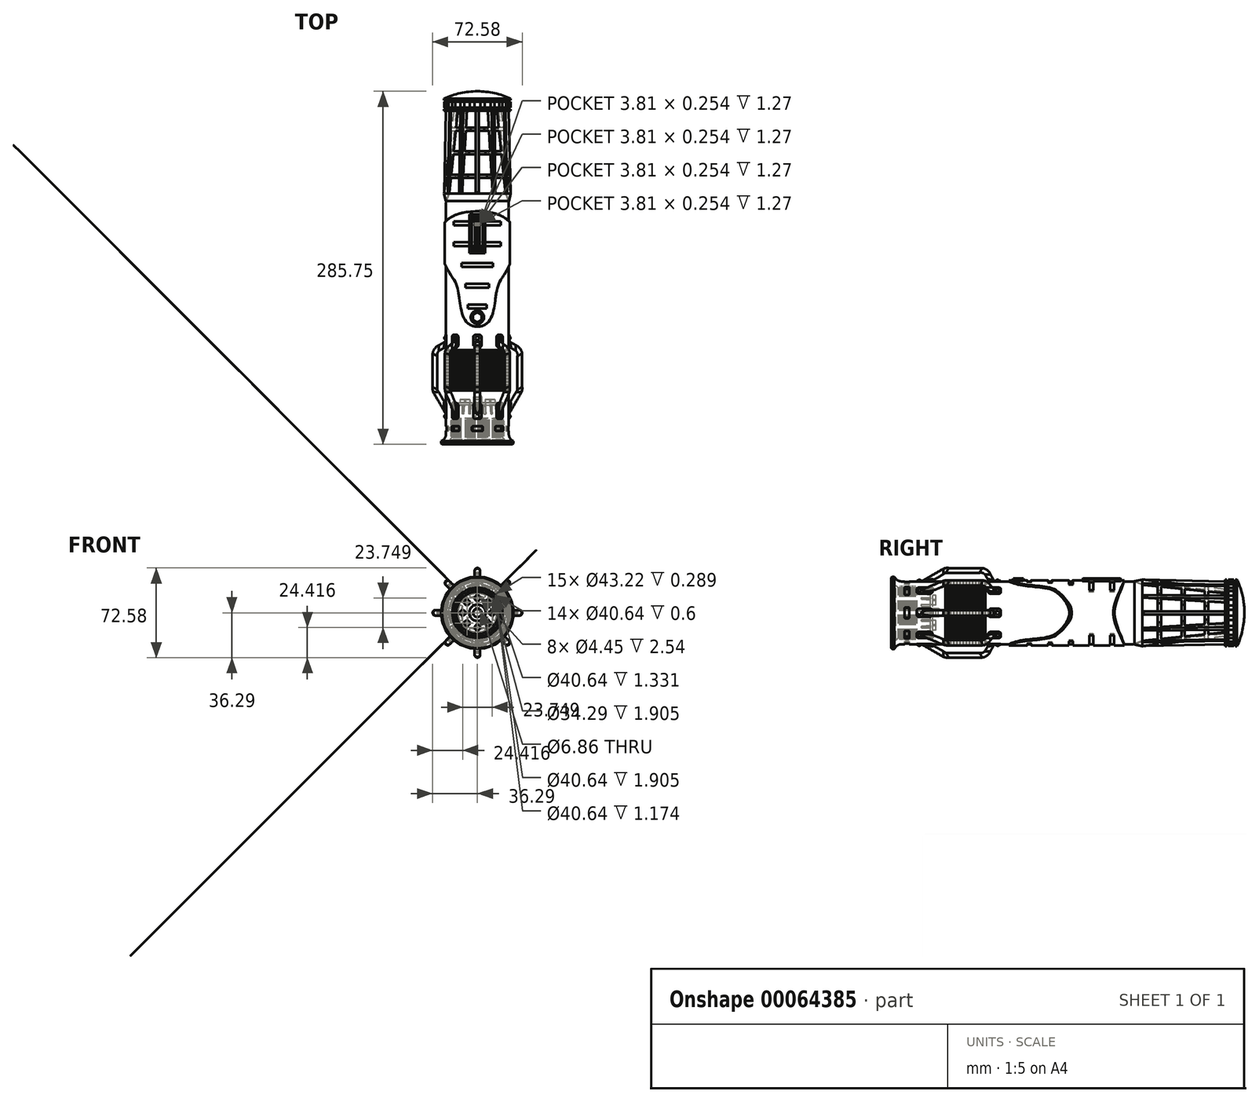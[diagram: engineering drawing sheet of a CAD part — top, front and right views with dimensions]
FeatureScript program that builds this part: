
annotation { "Feature Type Name" : "Feature", "Feature Type Description" : "" }
export const myFeature = defineFeature(function(context is Context, id is Id, definition is map)
    precondition{}
    {
        {
            var Q0;
            Q0=qCreatedBy(makeId("Right.planeOp"),FACE);
            var sketch = newSketch(context, id + "F0", { "sketchPlane" : qUnion([Q0])});
            skLineSegment(sketch, "E0", {"start": v(44.04, 0) * mm, "end": v(254, 0) * mm});
            skLineSegment(sketch, "E1", {"start": v(270.13, 19.05) * mm, "end": v(256.42, 20.68) * mm});
            skLineSegment(sketch, "E2", {"start": v(203, 27.02) * mm, "end": v(196.97, 25.65) * mm});
            skLineSegment(sketch, "E3", {"start": v(195.42, 25.4) * mm, "end": v(76.16, 25.4) * mm});
            skLineSegment(sketch, "E4", {"start": v(0, 25.4) * mm, "end": v(0, 20.32) * mm});
            skLineSegment(sketch, "E5", {"start": v(254, 0) * mm, "end": v(285.75, 0) * mm});
            skPoint(sketch, "E6.visualSharp", {"position": v(270.13, 19.05) * mm});
            skLineSegment(sketch, "E7", {"start": v(0, 25.4) * mm, "end": v(0, 29.21) * mm});
            skLineSegment(sketch, "E8", {"start": v(0, 29.21) * mm, "end": v(2.54, 29.21) * mm});
            skLineSegment(sketch, "E9", {"start": v(2.54, 29.21) * mm, "end": v(4.74, 25.4) * mm});
            skLineSegment(sketch, "E10", {"start": v(31.75, 3.43) * mm, "end": v(31.75, 6.6) * mm});
            skLineSegment(sketch, "E11", {"start": v(20.95, 20.32) * mm, "end": v(19.62, 20.32) * mm});
            skLineSegment(sketch, "E12", {"start": v(1.9, 20.32) * mm, "end": v(3.8, 22.23) * mm});
            skLineSegment(sketch, "E13", {"start": v(3.81, 22.23) * mm, "end": v(5.72, 20.32) * mm});
            skLineSegment(sketch, "E14", {"start": v(6.89, 20.32) * mm, "end": v(6.89, 21.61) * mm});
            skLineSegment(sketch, "E15", {"start": v(6.89, 21.61) * mm, "end": v(7.18, 21.61) * mm});
            skLineSegment(sketch, "E16", {"start": v(7.18, 21.61) * mm, "end": v(7.18, 20.32) * mm});
            skLineSegment(sketch, "E17.1.0.0", {"start": v(7.78, 20.32) * mm, "end": v(7.78, 21.61) * mm});
            skLineSegment(sketch, "E17.1.0.1", {"start": v(7.78, 21.61) * mm, "end": v(8.07, 21.61) * mm});
            skLineSegment(sketch, "E17.1.0.2", {"start": v(8.07, 21.61) * mm, "end": v(8.07, 20.32) * mm});
            skLineSegment(sketch, "E17.2.0.0", {"start": v(8.67, 20.32) * mm, "end": v(8.67, 21.61) * mm});
            skLineSegment(sketch, "E17.2.0.1", {"start": v(8.67, 21.61) * mm, "end": v(8.96, 21.61) * mm});
            skLineSegment(sketch, "E17.2.0.2", {"start": v(8.96, 21.61) * mm, "end": v(8.96, 20.32) * mm});
            skLineSegment(sketch, "E17.3.0.0", {"start": v(9.56, 20.32) * mm, "end": v(9.56, 21.61) * mm});
            skLineSegment(sketch, "E17.3.0.1", {"start": v(9.56, 21.61) * mm, "end": v(9.85, 21.61) * mm});
            skLineSegment(sketch, "E17.3.0.2", {"start": v(9.85, 21.61) * mm, "end": v(9.85, 20.32) * mm});
            skLineSegment(sketch, "E17.4.0.0", {"start": v(10.45, 20.32) * mm, "end": v(10.45, 21.61) * mm});
            skLineSegment(sketch, "E17.4.0.1", {"start": v(10.45, 21.61) * mm, "end": v(10.73, 21.61) * mm});
            skLineSegment(sketch, "E17.4.0.2", {"start": v(10.73, 21.61) * mm, "end": v(10.73, 20.32) * mm});
            skLineSegment(sketch, "E17.5.0.0", {"start": v(11.33, 20.32) * mm, "end": v(11.33, 21.61) * mm});
            skLineSegment(sketch, "E17.5.0.1", {"start": v(11.33, 21.61) * mm, "end": v(11.62, 21.61) * mm});
            skLineSegment(sketch, "E17.5.0.2", {"start": v(11.62, 21.61) * mm, "end": v(11.62, 20.32) * mm});
            skLineSegment(sketch, "E17.6.0.0", {"start": v(12.22, 20.32) * mm, "end": v(12.22, 21.61) * mm});
            skLineSegment(sketch, "E17.6.0.1", {"start": v(12.22, 21.61) * mm, "end": v(12.51, 21.61) * mm});
            skLineSegment(sketch, "E17.6.0.2", {"start": v(12.51, 21.61) * mm, "end": v(12.51, 20.32) * mm});
            skLineSegment(sketch, "E17.7.0.0", {"start": v(13.11, 20.32) * mm, "end": v(13.11, 21.61) * mm});
            skLineSegment(sketch, "E17.7.0.1", {"start": v(13.11, 21.61) * mm, "end": v(13.4, 21.61) * mm});
            skLineSegment(sketch, "E17.7.0.2", {"start": v(13.4, 21.61) * mm, "end": v(13.4, 20.32) * mm});
            skLineSegment(sketch, "E17.8.0.0", {"start": v(14, 20.32) * mm, "end": v(14, 21.61) * mm});
            skLineSegment(sketch, "E17.8.0.1", {"start": v(14, 21.61) * mm, "end": v(14.3, 21.61) * mm});
            skLineSegment(sketch, "E17.8.0.2", {"start": v(14.3, 21.61) * mm, "end": v(14.3, 20.32) * mm});
            skLineSegment(sketch, "E17.9.0.0", {"start": v(14.9, 20.32) * mm, "end": v(14.9, 21.61) * mm});
            skLineSegment(sketch, "E17.9.0.1", {"start": v(14.9, 21.61) * mm, "end": v(15.18, 21.61) * mm});
            skLineSegment(sketch, "E17.9.0.2", {"start": v(15.18, 21.61) * mm, "end": v(15.18, 20.32) * mm});
            skLineSegment(sketch, "E17.10.0.0", {"start": v(15.78, 20.32) * mm, "end": v(15.78, 21.61) * mm});
            skLineSegment(sketch, "E17.10.0.1", {"start": v(15.78, 21.61) * mm, "end": v(16.07, 21.61) * mm});
            skLineSegment(sketch, "E17.10.0.2", {"start": v(16.07, 21.61) * mm, "end": v(16.07, 20.32) * mm});
            skLineSegment(sketch, "E17.11.0.0", {"start": v(16.67, 20.32) * mm, "end": v(16.67, 21.61) * mm});
            skLineSegment(sketch, "E17.11.0.1", {"start": v(16.67, 21.61) * mm, "end": v(16.96, 21.61) * mm});
            skLineSegment(sketch, "E17.11.0.2", {"start": v(16.96, 21.61) * mm, "end": v(16.96, 20.32) * mm});
            skLineSegment(sketch, "E17.12.0.0", {"start": v(17.56, 20.32) * mm, "end": v(17.56, 21.61) * mm});
            skLineSegment(sketch, "E17.12.0.1", {"start": v(17.56, 21.61) * mm, "end": v(17.85, 21.61) * mm});
            skLineSegment(sketch, "E17.12.0.2", {"start": v(17.85, 21.61) * mm, "end": v(17.85, 20.32) * mm});
            skLineSegment(sketch, "E17.13.0.0", {"start": v(18.45, 20.32) * mm, "end": v(18.45, 21.61) * mm});
            skLineSegment(sketch, "E17.13.0.1", {"start": v(18.45, 21.61) * mm, "end": v(18.74, 21.61) * mm});
            skLineSegment(sketch, "E17.13.0.2", {"start": v(18.74, 21.61) * mm, "end": v(18.74, 20.32) * mm});
            skLineSegment(sketch, "E17.14.0.0", {"start": v(19.34, 20.32) * mm, "end": v(19.34, 21.61) * mm});
            skLineSegment(sketch, "E17.14.0.1", {"start": v(19.34, 21.61) * mm, "end": v(19.62, 21.61) * mm});
            skLineSegment(sketch, "E17.14.0.2", {"start": v(19.62, 21.61) * mm, "end": v(19.62, 20.32) * mm});
            skLineSegment(sketch, "E17.direction1", {"start": v(7.18, 20.32) * mm, "end": v(7.78, 20.32) * mm, "construction": true});
            skLineSegment(sketch, "E18", {"start": v(31.75, 3.43) * mm, "end": v(38.1, 3.43) * mm});
            skLineSegment(sketch, "E19", {"start": v(38.1, 3.43) * mm, "end": v(44.04, 0) * mm});
            skLineSegment(sketch, "E20.bottom", {"start": v(31.75, 17.15) * mm, "end": v(33.65, 17.15) * mm});
            skLineSegment(sketch, "E20.top", {"start": v(31.75, 6.6) * mm, "end": v(33.65, 6.6) * mm});
            skLineSegment(sketch, "E20.right", {"start": v(33.65, 17.15) * mm, "end": v(33.65, 6.6) * mm});
            skLineSegment(sketch, "E21", {"start": v(31.75, 18.42) * mm, "end": v(20.95, 20.32) * mm});
            skPoint(sketch, "E22.orphan", {"position": v(31.75, 20.32) * mm});
            skLineSegment(sketch, "E23.trimOffspring", {"start": v(31.75, 17.15) * mm, "end": v(31.75, 18.42) * mm});
            skLineSegment(sketch, "E24.trimOffspring", {"start": v(6.89, 20.32) * mm, "end": v(5.71, 20.32) * mm});
            skLineSegment(sketch, "E25.trimOffspring", {"start": v(7.78, 20.32) * mm, "end": v(7.18, 20.32) * mm});
            skLineSegment(sketch, "E26.trimOffspring", {"start": v(8.67, 20.32) * mm, "end": v(8.07, 20.32) * mm});
            skLineSegment(sketch, "E27.trimOffspring", {"start": v(9.56, 20.32) * mm, "end": v(8.96, 20.32) * mm});
            skLineSegment(sketch, "E28.trimOffspring", {"start": v(10.45, 20.32) * mm, "end": v(9.85, 20.32) * mm});
            skLineSegment(sketch, "E29.trimOffspring", {"start": v(11.33, 20.32) * mm, "end": v(10.73, 20.32) * mm});
            skLineSegment(sketch, "E30.trimOffspring", {"start": v(12.22, 20.32) * mm, "end": v(11.62, 20.32) * mm});
            skLineSegment(sketch, "E31.trimOffspring", {"start": v(13.11, 20.32) * mm, "end": v(12.51, 20.32) * mm});
            skLineSegment(sketch, "E32.trimOffspring", {"start": v(14, 20.32) * mm, "end": v(13.4, 20.32) * mm});
            skLineSegment(sketch, "E33.trimOffspring", {"start": v(14.9, 20.32) * mm, "end": v(14.3, 20.32) * mm});
            skLineSegment(sketch, "E34.trimOffspring", {"start": v(15.78, 20.32) * mm, "end": v(15.18, 20.32) * mm});
            skLineSegment(sketch, "E35.trimOffspring", {"start": v(16.67, 20.32) * mm, "end": v(16.07, 20.32) * mm});
            skLineSegment(sketch, "E36.trimOffspring", {"start": v(17.56, 20.32) * mm, "end": v(16.96, 20.32) * mm});
            skLineSegment(sketch, "E37.trimOffspring", {"start": v(18.45, 20.32) * mm, "end": v(17.85, 20.32) * mm});
            skLineSegment(sketch, "E38.trimOffspring", {"start": v(19.34, 20.32) * mm, "end": v(18.74, 20.32) * mm});
            skLineSegment(sketch, "E39.trimOffspring", {"start": v(1.9, 20.32) * mm, "end": v(0, 20.32) * mm});
            skPoint(sketch, "E40.orphan", {"position": v(0, 0) * mm});
            skLineSegment(sketch, "E41.top", {"start": v(44.04, 26.04) * mm, "end": v(45.3, 26.04) * mm});
            skLineSegment(sketch, "E42", {"start": v(44.04, 26.04) * mm, "end": v(43.67, 25.4) * mm});
            skLineSegment(sketch, "E43", {"start": v(75.79, 26.04) * mm, "end": v(76.16, 25.4) * mm});
            skLineSegment(sketch, "E44", {"start": v(45.3, 26.04) * mm, "end": v(45.3, 26.1) * mm});
            skLineSegment(sketch, "E45", {"start": v(45.82, 26.1) * mm, "end": v(45.82, 26.04) * mm});
            skArc(sketch, "E46", {"start": v(45.82, 26.1) * mm, "mid": v(45.56, 26.35) * mm, "end": v(45.3, 26.1) * mm});
            skLineSegment(sketch, "E47.1.0.0", {"start": v(47.85, 26.04) * mm, "end": v(47.85, 26.1) * mm});
            skArc(sketch, "E47.1.0.1", {"start": v(48.36, 26.1) * mm, "mid": v(48.1, 26.35) * mm, "end": v(47.85, 26.1) * mm});
            skLineSegment(sketch, "E47.1.0.2", {"start": v(48.36, 26.1) * mm, "end": v(48.36, 26.04) * mm});
            skLineSegment(sketch, "E47.2.0.0", {"start": v(50.39, 26.04) * mm, "end": v(50.39, 26.1) * mm});
            skArc(sketch, "E47.2.0.1", {"start": v(50.9, 26.1) * mm, "mid": v(50.64, 26.35) * mm, "end": v(50.39, 26.1) * mm});
            skLineSegment(sketch, "E47.2.0.2", {"start": v(50.9, 26.1) * mm, "end": v(50.9, 26.04) * mm});
            skLineSegment(sketch, "E47.3.0.0", {"start": v(52.93, 26.04) * mm, "end": v(52.93, 26.1) * mm});
            skArc(sketch, "E47.3.0.1", {"start": v(53.44, 26.1) * mm, "mid": v(53.18, 26.35) * mm, "end": v(52.93, 26.1) * mm});
            skLineSegment(sketch, "E47.3.0.2", {"start": v(53.44, 26.1) * mm, "end": v(53.44, 26.04) * mm});
            skLineSegment(sketch, "E47.4.0.0", {"start": v(55.47, 26.04) * mm, "end": v(55.47, 26.1) * mm});
            skArc(sketch, "E47.4.0.1", {"start": v(55.98, 26.1) * mm, "mid": v(55.72, 26.35) * mm, "end": v(55.47, 26.1) * mm});
            skLineSegment(sketch, "E47.4.0.2", {"start": v(55.98, 26.1) * mm, "end": v(55.98, 26.04) * mm});
            skLineSegment(sketch, "E47.5.0.0", {"start": v(58, 26.04) * mm, "end": v(58, 26.1) * mm});
            skArc(sketch, "E47.5.0.1", {"start": v(58.52, 26.1) * mm, "mid": v(58.26, 26.35) * mm, "end": v(58, 26.1) * mm});
            skLineSegment(sketch, "E47.5.0.2", {"start": v(58.52, 26.1) * mm, "end": v(58.52, 26.04) * mm});
            skLineSegment(sketch, "E47.6.0.0", {"start": v(60.55, 26.04) * mm, "end": v(60.55, 26.1) * mm});
            skArc(sketch, "E47.6.0.1", {"start": v(61.06, 26.1) * mm, "mid": v(60.8, 26.35) * mm, "end": v(60.55, 26.1) * mm});
            skLineSegment(sketch, "E47.6.0.2", {"start": v(61.06, 26.1) * mm, "end": v(61.06, 26.04) * mm});
            skLineSegment(sketch, "E47.7.0.0", {"start": v(63.09, 26.04) * mm, "end": v(63.09, 26.1) * mm});
            skArc(sketch, "E47.7.0.1", {"start": v(63.6, 26.1) * mm, "mid": v(63.34, 26.35) * mm, "end": v(63.09, 26.1) * mm});
            skLineSegment(sketch, "E47.7.0.2", {"start": v(63.6, 26.1) * mm, "end": v(63.6, 26.04) * mm});
            skLineSegment(sketch, "E47.8.0.0", {"start": v(65.63, 26.04) * mm, "end": v(65.63, 26.1) * mm});
            skArc(sketch, "E47.8.0.1", {"start": v(66.14, 26.1) * mm, "mid": v(65.88, 26.35) * mm, "end": v(65.63, 26.1) * mm});
            skLineSegment(sketch, "E47.8.0.2", {"start": v(66.14, 26.1) * mm, "end": v(66.14, 26.04) * mm});
            skLineSegment(sketch, "E47.9.0.0", {"start": v(68.17, 26.04) * mm, "end": v(68.17, 26.1) * mm});
            skArc(sketch, "E47.9.0.1", {"start": v(68.68, 26.1) * mm, "mid": v(68.42, 26.35) * mm, "end": v(68.17, 26.1) * mm});
            skLineSegment(sketch, "E47.9.0.2", {"start": v(68.68, 26.1) * mm, "end": v(68.68, 26.04) * mm});
            skLineSegment(sketch, "E47.10.0.0", {"start": v(70.7, 26.04) * mm, "end": v(70.7, 26.1) * mm});
            skArc(sketch, "E47.10.0.1", {"start": v(71.22, 26.1) * mm, "mid": v(70.96, 26.35) * mm, "end": v(70.7, 26.1) * mm});
            skLineSegment(sketch, "E47.10.0.2", {"start": v(71.22, 26.1) * mm, "end": v(71.22, 26.04) * mm});
            skLineSegment(sketch, "E47.11.0.0", {"start": v(73.25, 26.04) * mm, "end": v(73.25, 26.1) * mm});
            skArc(sketch, "E47.11.0.1", {"start": v(73.76, 26.1) * mm, "mid": v(73.5, 26.35) * mm, "end": v(73.25, 26.1) * mm});
            skLineSegment(sketch, "E47.11.0.2", {"start": v(73.76, 26.1) * mm, "end": v(73.76, 26.04) * mm});
            skLineSegment(sketch, "E47.direction1", {"start": v(45.3, 26.04) * mm, "end": v(47.85, 26.04) * mm, "construction": true});
            skLineSegment(sketch, "E48.trimOffspring", {"start": v(45.82, 26.04) * mm, "end": v(47.85, 26.04) * mm});
            skLineSegment(sketch, "E49.trimOffspring", {"start": v(48.36, 26.04) * mm, "end": v(50.39, 26.04) * mm});
            skLineSegment(sketch, "E50.trimOffspring", {"start": v(50.9, 26.04) * mm, "end": v(52.93, 26.04) * mm});
            skLineSegment(sketch, "E51.trimOffspring", {"start": v(53.44, 26.04) * mm, "end": v(55.47, 26.04) * mm});
            skLineSegment(sketch, "E52.trimOffspring", {"start": v(55.98, 26.04) * mm, "end": v(58, 26.04) * mm});
            skLineSegment(sketch, "E53.trimOffspring", {"start": v(58.52, 26.04) * mm, "end": v(60.55, 26.04) * mm});
            skLineSegment(sketch, "E54.trimOffspring", {"start": v(61.06, 26.04) * mm, "end": v(63.09, 26.04) * mm});
            skLineSegment(sketch, "E55.trimOffspring", {"start": v(63.6, 26.04) * mm, "end": v(65.63, 26.04) * mm});
            skLineSegment(sketch, "E56.trimOffspring", {"start": v(66.14, 26.04) * mm, "end": v(68.17, 26.04) * mm});
            skLineSegment(sketch, "E57.trimOffspring", {"start": v(68.68, 26.04) * mm, "end": v(70.7, 26.04) * mm});
            skLineSegment(sketch, "E58.trimOffspring", {"start": v(71.22, 26.04) * mm, "end": v(73.25, 26.04) * mm});
            skLineSegment(sketch, "E59.trimOffspring", {"start": v(73.76, 26.04) * mm, "end": v(75.79, 26.04) * mm});
            skLineSegment(sketch, "E60.trimOffspring", {"start": v(43.67, 25.4) * mm, "end": v(4.74, 25.4) * mm});
            skPoint(sketch, "E41.left.start.orphan", {"position": v(44.04, 25.4) * mm});
            skLineSegment(sketch, "E61", {"start": v(196.3, 25.25) * mm, "end": v(203.03, 22.8) * mm});
            skLineSegment(sketch, "E62", {"start": v(203.03, 22.8) * mm, "end": v(203.03, 23.2) * mm});
            skLineSegment(sketch, "E63", {"start": v(203.03, 23.2) * mm, "end": v(196.96, 25.4) * mm});
            skPoint(sketch, "E64.visualSharp", {"position": v(195.87, 25.4) * mm});
            skArc(sketch, "E64.filletArc", {"start": v(196.3, 25.25) * mm, "mid": v(195.86, 25.36) * mm, "end": v(195.42, 25.4) * mm});
            skPoint(sketch, "E65.visualSharp", {"position": v(196.55, 25.56) * mm});
            skArc(sketch, "E65.filletArc", {"start": v(196.97, 25.65) * mm, "mid": v(196.88, 25.54) * mm, "end": v(196.96, 25.4) * mm});
            skArc(sketch, "E66", {"start": v(285.75, 0) * mm, "mid": v(284.22, 13.84) * mm, "end": v(279.71, 27.02) * mm});
            skLineSegment(sketch, "E67", {"start": v(270.13, 19.05) * mm, "end": v(270.13, 27.02) * mm});
            skLineSegment(sketch, "E68", {"start": v(270.13, 27.02) * mm, "end": v(271.4, 27.02) * mm});
            skLineSegment(sketch, "E69", {"start": v(271.4, 27.02) * mm, "end": v(271.4, 24.86) * mm});
            skLineSegment(sketch, "E70", {"start": v(271.4, 24.86) * mm, "end": v(272.67, 24.86) * mm});
            skLineSegment(sketch, "E71", {"start": v(272.67, 24.86) * mm, "end": v(272.67, 27.02) * mm});
            skLineSegment(sketch, "E72", {"start": v(272.67, 27.02) * mm, "end": v(277.17, 27.02) * mm});
            skLineSegment(sketch, "E73", {"start": v(277.17, 27.02) * mm, "end": v(277.17, 24.86) * mm});
            skLineSegment(sketch, "E74", {"start": v(277.17, 24.86) * mm, "end": v(278.44, 24.86) * mm});
            skLineSegment(sketch, "E75", {"start": v(278.44, 24.86) * mm, "end": v(278.44, 27.02) * mm});
            skLineSegment(sketch, "E76.trimOffspring", {"start": v(278.44, 27.02) * mm, "end": v(279.71, 27.02) * mm});
            skLineSegment(sketch, "E77.top", {"start": v(215.7, 17.9) * mm, "end": v(218.32, 17.9) * mm});
            skLineSegment(sketch, "E77.left", {"start": v(215.7, 25.51) * mm, "end": v(215.7, 17.9) * mm});
            skLineSegment(sketch, "E77.right", {"start": v(218.32, 25.2) * mm, "end": v(218.32, 17.9) * mm});
            skLineSegment(sketch, "E78.1.0.0", {"start": v(234.75, 23.25) * mm, "end": v(234.75, 15.63) * mm});
            skLineSegment(sketch, "E78.1.0.1", {"start": v(237.37, 22.94) * mm, "end": v(237.37, 15.63) * mm});
            skLineSegment(sketch, "E78.1.0.2", {"start": v(234.75, 15.63) * mm, "end": v(237.37, 15.63) * mm});
            skLineSegment(sketch, "E78.2.0.0", {"start": v(253.8, 20.99) * mm, "end": v(253.8, 13.37) * mm});
            skLineSegment(sketch, "E78.2.0.1", {"start": v(256.42, 20.68) * mm, "end": v(256.42, 13.37) * mm});
            skLineSegment(sketch, "E78.2.0.2", {"start": v(253.8, 13.37) * mm, "end": v(256.42, 13.37) * mm});
            skLineSegment(sketch, "E79.trimOffspring", {"start": v(215.7, 25.51) * mm, "end": v(203, 27.02) * mm});
            skPoint(sketch, "E80.orphan", {"position": v(218.32, 26.14) * mm});
            skPoint(sketch, "E81.orphan", {"position": v(215.7, 29.67) * mm});
            skPoint(sketch, "E82.orphan", {"position": v(234.75, 29.67) * mm});
            skPoint(sketch, "E83.orphan", {"position": v(237.37, 24.63) * mm});
            skLineSegment(sketch, "E84.trimOffspring", {"start": v(234.75, 23.25) * mm, "end": v(218.32, 25.2) * mm});
            skPoint(sketch, "E85.orphan", {"position": v(253.8, 28.16) * mm});
            skLineSegment(sketch, "E86.trimOffspring", {"start": v(253.8, 20.99) * mm, "end": v(237.37, 22.94) * mm});
            skPoint(sketch, "E87.orphan", {"position": v(256.42, 22.37) * mm});
            skSolve(sketch);
        }
        {
            var Q0;
            Q0 = qSketchRegion(id + "F0", true);
            var Q1;
            Q1=sQuery(id+"F0.wireOp",EDGE,"E0");
            revolve(context, id + "F1", {"entities" : qUnion([Q0]), "axis" : qUnion([Q1]), "revolveType" : RevolveType.FULL});
        }
        {
            var Q0;
            Q0=qCreatedBy(makeId("Top.planeOp"),FACE);
            var sketch = newSketch(context, id + "F2", { "sketchPlane" : qUnion([Q0])});
            skFitSpline(sketch, "E88", {"points": [v(0, 95.25) * mm, v(18.97, 133.22) * mm], "startDerivative": vector(53.75, 1.68) * mm, "endDerivative": vector(22.66, 34.25) * mm});
            skFitSpline(sketch, "E89", {"points": [v(18.97, 133.22) * mm, v(0, 188.6) * mm], "startDerivative": vector(48.26, 68.65) * mm, "endDerivative": vector(-122.9, 0.45) * mm});
            skLineSegment(sketch, "E90.bottom", {"start": v(0, 180.34) * mm, "end": v(19.05, 180.34) * mm});
            skLineSegment(sketch, "E90.top", {"start": v(0, 177.16) * mm, "end": v(19.05, 177.16) * mm});
            skLineSegment(sketch, "E90.right", {"start": v(19.05, 180.34) * mm, "end": v(19.05, 177.16) * mm});
            skLineSegment(sketch, "E91.bottom", {"start": v(0, 163.58) * mm, "end": v(19.05, 163.58) * mm});
            skLineSegment(sketch, "E91.top", {"start": v(0, 160.4) * mm, "end": v(19.05, 160.4) * mm});
            skLineSegment(sketch, "E91.right", {"start": v(19.05, 163.58) * mm, "end": v(19.05, 160.4) * mm});
            skLineSegment(sketch, "E92.bottom", {"start": v(0, 146.81) * mm, "end": v(12.7, 146.81) * mm});
            skLineSegment(sketch, "E92.top", {"start": v(0, 143.64) * mm, "end": v(12.7, 143.64) * mm});
            skLineSegment(sketch, "E92.right", {"start": v(12.7, 146.81) * mm, "end": v(12.7, 143.64) * mm});
            skLineSegment(sketch, "E93.bottom", {"start": v(0, 130.05) * mm, "end": v(9.53, 130.05) * mm});
            skLineSegment(sketch, "E93.top", {"start": v(0, 126.87) * mm, "end": v(9.53, 126.87) * mm});
            skLineSegment(sketch, "E93.right", {"start": v(9.53, 130.05) * mm, "end": v(9.53, 126.87) * mm});
            skLineSegment(sketch, "E94.bottom", {"start": v(0, 113.28) * mm, "end": v(7.62, 113.28) * mm});
            skLineSegment(sketch, "E94.top", {"start": v(0, 110.1) * mm, "end": v(7.62, 110.1) * mm});
            skLineSegment(sketch, "E94.right", {"start": v(7.62, 113.28) * mm, "end": v(7.62, 110.1) * mm});
            skPoint(sketch, "E95.orphan", {"position": v(9.53, 110.1) * mm});
            skFitSpline(sketch, "E96.MirrorCS", {"points": [v(-18.97, 133.22) * mm, v(0, 188.6) * mm], "startDerivative": vector(-48.26, 68.65) * mm, "endDerivative": vector(122.9, 0.45) * mm});
            skFitSpline(sketch, "E97.MirrorCS", {"points": [v(0, 95.25) * mm, v(-18.97, 133.22) * mm], "startDerivative": vector(-53.75, 1.68) * mm, "endDerivative": vector(-22.66, 34.25) * mm});
            skLineSegment(sketch, "E98.MirrorCS", {"start": v(0, 110.1) * mm, "end": v(-7.62, 110.1) * mm});
            skLineSegment(sketch, "E99.MirrorCS", {"start": v(-7.62, 113.28) * mm, "end": v(-7.62, 110.1) * mm});
            skLineSegment(sketch, "E100.MirrorCS", {"start": v(0, 113.28) * mm, "end": v(-7.62, 113.28) * mm});
            skLineSegment(sketch, "E101.MirrorCS", {"start": v(0, 126.87) * mm, "end": v(-9.53, 126.87) * mm});
            skLineSegment(sketch, "E102.MirrorCS", {"start": v(-9.53, 130.05) * mm, "end": v(-9.53, 126.87) * mm});
            skLineSegment(sketch, "E103.MirrorCS", {"start": v(0, 130.05) * mm, "end": v(-9.53, 130.05) * mm});
            skLineSegment(sketch, "E104.MirrorCS", {"start": v(0, 143.64) * mm, "end": v(-12.7, 143.64) * mm});
            skLineSegment(sketch, "E105.MirrorCS", {"start": v(-12.7, 146.81) * mm, "end": v(-12.7, 143.64) * mm});
            skLineSegment(sketch, "E106.MirrorCS", {"start": v(0, 146.81) * mm, "end": v(-12.7, 146.81) * mm});
            skLineSegment(sketch, "E107.MirrorCS", {"start": v(0, 160.4) * mm, "end": v(-19.05, 160.4) * mm});
            skLineSegment(sketch, "E108.MirrorCS", {"start": v(-19.05, 163.58) * mm, "end": v(-19.05, 160.4) * mm});
            skLineSegment(sketch, "E109.MirrorCS", {"start": v(0, 163.58) * mm, "end": v(-19.05, 163.58) * mm});
            skLineSegment(sketch, "E110.MirrorCS", {"start": v(0, 177.16) * mm, "end": v(-19.05, 177.16) * mm});
            skLineSegment(sketch, "E111.MirrorCS", {"start": v(-19.05, 180.34) * mm, "end": v(-19.05, 177.16) * mm});
            skLineSegment(sketch, "E112.MirrorCS", {"start": v(0, 180.34) * mm, "end": v(-19.05, 180.34) * mm});
            skSolve(sketch);
        }
        {
            var Q0;
            Q0 = qSketchRegion(id + "F2", true);
            extrude(context, id + "F3", {"entities" : qUnion([Q0]), "operationType" : NewBodyOperationType.ADD, "depth" : 30.48 * mm, "hasSecondDirection" : true, "secondDirectionOppositeDirection" : true, "secondDirectionDepth" : 30.48 * mm});
        }
        {
            var Q0;
            Q0=qCreatedBy(makeId("Front.planeOp"),FACE);
            cPlane(context, id + "F4", {"entities" : qUnion([Q0]), "cplaneType" : CPlaneType.OFFSET, "offset" : 91.44 * mm, "oppositeDirection" : true, "width" : 152.4 * mm, "height" : 152.4 * mm});
        }
        {
            var Q0;
            Q0=qCreatedBy(id+"F4.planeOp",FACE);
            var sketch = newSketch(context, id + "F5", { "sketchPlane" : qUnion([Q0])});
            skCircle(sketch, "E113", {"center": v(0, 0) * mm, "radius": 26.35 * mm});
            skCircle(sketch, "E114", {"center": v(0, 0) * mm, "radius": 49.48 * mm});
            skSolve(sketch);
        }
        {
            var Q0;
            Q0 = qSketchRegion(id + "F5", true);
            extrude(context, id + "F6", {"entities" : qUnion([Q0]), "operationType" : NewBodyOperationType.REMOVE, "oppositeDirection" : true, "depth" : 99.06 * mm});
        }
        {
            var Q0;
            Q0=qCreatedBy(makeId("Right.planeOp"),FACE);
            var sketch = newSketch(context, id + "F7", { "sketchPlane" : qUnion([Q0])});
            skLineSegment(sketch, "E115", {"start": v(23.88, 22.86) * mm, "end": v(42.2, 33.44) * mm});
            skLineSegment(sketch, "E116", {"start": v(45.37, 34.3) * mm, "end": v(72.49, 34.3) * mm});
            skLineSegment(sketch, "E117", {"start": v(77.99, 31.11) * mm, "end": v(82.75, 22.86) * mm});
            skPoint(sketch, "E118.visualSharp", {"position": v(76.16, 34.3) * mm});
            skArc(sketch, "E118.filletArc", {"start": v(77.99, 31.12) * mm, "mid": v(75.66, 33.44) * mm, "end": v(72.49, 34.3) * mm});
            skPoint(sketch, "E119.visualSharp", {"position": v(43.67, 34.3) * mm});
            skArc(sketch, "E119.filletArc", {"start": v(45.37, 34.3) * mm, "mid": v(43.73, 34.07) * mm, "end": v(42.2, 33.44) * mm});
            skSolve(sketch);
        }
        {
            var Q0;
            Q0=qCreatedBy(makeId("Top.planeOp"),FACE);
            cPlane(context, id + "F8", {"entities" : qUnion([Q0]), "cplaneType" : CPlaneType.OFFSET, "offset" : 22.86 * mm, "width" : 152.4 * mm, "height" : 152.4 * mm});
        }
        {
            var Q0;
            Q0=qCreatedBy(id+"F8.planeOp",FACE);
            var sketch = newSketch(context, id + "F9", { "sketchPlane" : qUnion([Q0])});
            skCircle(sketch, "E120", {"center": v(0, 82.75) * mm, "radius": 2.22 * mm});
            skSolve(sketch);
        }
        {
            var Q0;
            Q0 = qSketchRegion(id + "F9", true);
            var Q1;
            Q1 = qConstructionFilter(qBodyType(qCreatedBy(id + "F7" ,EDGE), BodyType.WIRE), ConstructionObject.NO);
            sweep(context, id + "F10", {"profiles" : qUnion([Q0]), "path" : qUnion([Q1])});
        }
        {
            var Q0;
            Q0=qCreatedBy(makeId("Right.planeOp"),FACE);
            var sketch = newSketch(context, id + "F11", { "sketchPlane" : qUnion([Q0])});
            skLineSegment(sketch, "E121.bottom", {"start": v(20.62, 24.56) * mm, "end": v(33.32, 24.56) * mm});
            skLineSegment(sketch, "E121.top", {"start": v(20.62, 25.78) * mm, "end": v(33.32, 25.78) * mm});
            skLineSegment(sketch, "E121.left", {"start": v(20.62, 24.56) * mm, "end": v(20.62, 25.78) * mm});
            skLineSegment(sketch, "E121.right", {"start": v(33.32, 24.56) * mm, "end": v(33.32, 25.78) * mm});
            skLineSegment(sketch, "E122.bottom", {"start": v(78.5, 24.26) * mm, "end": v(88.67, 24.26) * mm});
            skLineSegment(sketch, "E122.top", {"start": v(78.5, 25.78) * mm, "end": v(88.67, 25.78) * mm});
            skLineSegment(sketch, "E122.left", {"start": v(78.5, 24.26) * mm, "end": v(78.5, 25.78) * mm});
            skLineSegment(sketch, "E122.right", {"start": v(88.67, 24.26) * mm, "end": v(88.67, 25.78) * mm});
            skLineSegment(sketch, "E123", {"start": v(0, 0) * mm, "end": v(95.37, 0) * mm});
            skSolve(sketch);
        }
        {
            var Q0;
            Q0 = qSketchRegion(id + "F11", true);
            var Q1;
            Q1=sQuery(id+"F11.wireOp",EDGE,"E123");
            revolve(context, id + "F12", {"entities" : qUnion([Q0]), "axis" : qUnion([Q1]), "revolveType" : RevolveType.SYMMETRIC, "angle" : 15 * degree});
        }
        {
            var Q0;
            Q0=makeQuery(id+"F12.opRevolve","CAP_EDGE",EDGE,{"disambiguationData":[OSD([sQuery(id+"F11.wireOp",EDGE,"E121.left")])],"isStart":false});
            var Q1;
            Q1=makeQuery(id+"F12.opRevolve","CAP_EDGE",EDGE,{"disambiguationData":[OSD([sQuery(id+"F11.wireOp",EDGE,"E121.right")])],"isStart":false});
            var Q2;
            Q2=makeQuery(id+"F12.opRevolve","CAP_EDGE",EDGE,{"disambiguationData":[OSD([sQuery(id+"F11.wireOp",EDGE,"E121.left")])],"isStart":true});
            var Q3;
            Q3=makeQuery(id+"F12.opRevolve","CAP_EDGE",EDGE,{"disambiguationData":[OSD([sQuery(id+"F11.wireOp",EDGE,"E121.right")])],"isStart":true});
            var Q4;
            Q4=makeQuery(id+"F12.opRevolve","CAP_EDGE",EDGE,{"disambiguationData":[OSD([sQuery(id+"F11.wireOp",EDGE,"E122.left")])],"isStart":false});
            var Q5;
            Q5=makeQuery(id+"F12.opRevolve","CAP_EDGE",EDGE,{"disambiguationData":[OSD([sQuery(id+"F11.wireOp",EDGE,"E122.left")])],"isStart":true});
            var Q6;
            Q6=makeQuery(id+"F12.opRevolve","CAP_EDGE",EDGE,{"disambiguationData":[OSD([sQuery(id+"F11.wireOp",EDGE,"E122.right")])],"isStart":false});
            var Q7;
            Q7=makeQuery(id+"F12.opRevolve","CAP_EDGE",EDGE,{"disambiguationData":[OSD([sQuery(id+"F11.wireOp",EDGE,"E122.right")])],"isStart":true});
            fillet(context, id + "F13", {"entities" : qUnion([Q0, Q1, Q2, Q3, Q4, Q5, Q6, Q7]), "radius" : 1.9 * mm, "tangentPropagation" : true, "allowEdgeOverflow" : false});
        }
        {
            var Q0;
            Q0=qCreatedBy(makeId("Right.planeOp"),FACE);
            var sketch = newSketch(context, id + "F14", { "sketchPlane" : qUnion([Q0])});
            skLineSegment(sketch, "E124", {"start": v(20.62, 25.78) * mm, "end": v(24.8, 25.78) * mm, "construction": true});
            skArc(sketch, "E125", {"start": v(22.71, 26.73) * mm, "mid": v(21, 25.02) * mm, "end": v(22.71, 23.3) * mm});
            skPoint(sketch, "E125.centerSnap0", {"position": v(22.71, 25.78) * mm});
            skLineSegment(sketch, "E126", {"start": v(22.71, 23.3) * mm, "end": v(22.71, 26.73) * mm});
            skSolve(sketch);
        }
        {
            var Q0;
            Q0 = qSketchRegion(id + "F14", true);
            var Q1;
            Q1=sQuery(id+"F14.wireOp",EDGE,"E126");
            revolve(context, id + "F15", {"entities" : qUnion([Q0]), "axis" : qUnion([Q1]), "revolveType" : RevolveType.FULL});
        }
        {
            var Q0;
            Q0=qCreatedBy(makeId("Right.planeOp"),FACE);
            var sketch = newSketch(context, id + "F16", { "sketchPlane" : qUnion([Q0])});
            skLineSegment(sketch, "E127", {"start": v(88.67, 25.78) * mm, "end": v(83.46, 25.78) * mm, "construction": true});
            skArc(sketch, "E128", {"start": v(86.07, 26.73) * mm, "mid": v(84.35, 25.02) * mm, "end": v(86.07, 23.3) * mm});
            skPoint(sketch, "E128.centerSnap0", {"position": v(86.07, 25.78) * mm});
            skLineSegment(sketch, "E129", {"start": v(86.07, 26.73) * mm, "end": v(86.07, 23.3) * mm});
            skSolve(sketch);
        }
        {
            var Q0;
            Q0 = qSketchRegion(id + "F16", true);
            var Q1;
            Q1=sQuery(id+"F16.wireOp",EDGE,"E129");
            revolve(context, id + "F17", {"entities" : qUnion([Q0]), "axis" : qUnion([Q1]), "revolveType" : RevolveType.FULL});
        }
        {
            var Q0;
            Q0=makeQuery(id+"F10.opSweep","SWEPT_BODY",BODY,{"disambiguationData":[OSD([sQuery(id+"F7.wireOp",EDGE,"E115"),sQuery(id+"F9.wireOp",EDGE,"E120")])]});
            var Q1;
            Q1=makeQuery(id+"F12.opRevolve","SWEPT_BODY",BODY,{"disambiguationData":[OSD([sQuery(id+"F11.wireOp",EDGE,"E121.bottom"),sQuery(id+"F11.wireOp",EDGE,"E121.top"),sQuery(id+"F11.wireOp",EDGE,"E121.left"),sQuery(id+"F11.wireOp",EDGE,"E121.right")])]});
            var Q2;
            Q2=makeQuery(id+"F15.opRevolve","SWEPT_BODY",BODY,{"disambiguationData":[OSD([sQuery(id+"F14.wireOp",EDGE,"E125"),sQuery(id+"F14.wireOp",EDGE,"E126")])]});
            var Q3;
            Q3=makeQuery(id+"F12.opRevolve","SWEPT_BODY",BODY,{"disambiguationData":[OSD([sQuery(id+"F11.wireOp",EDGE,"E122.bottom"),sQuery(id+"F11.wireOp",EDGE,"E122.top"),sQuery(id+"F11.wireOp",EDGE,"E122.left"),sQuery(id+"F11.wireOp",EDGE,"E122.right")])]});
            var Q4;
            Q4=makeQuery(id+"F17.opRevolve","SWEPT_BODY",BODY,{"disambiguationData":[OSD([sQuery(id+"F16.wireOp",EDGE,"E128"),sQuery(id+"F16.wireOp",EDGE,"E129")])]});
            var Q5;
            Q5=makeQuery(id+"F1.opRevolve","SWEPT_EDGE",EDGE,{"disambiguationData":[OSD([sQuery(id+"F0.wireOp",EDGE,"E7"),sQuery(id+"F0.wireOp",EDGE,"E8")])]});
            circularPattern(context, id + "F18", {"operationType" : NewBodyOperationType.ADD, "entities" : qUnion([Q0, Q1, Q2, Q3, Q4]), "axis" : qUnion([Q5]), "angle" : 45 * degree, "instanceCount" : 8});
        }
        {
            var Q0;
            Q0=qCreatedBy(makeId("Right.planeOp"),FACE);
            var sketch = newSketch(context, id + "F19", { "sketchPlane" : qUnion([Q0])});
            skLineSegment(sketch, "E130", {"start": v(203, 26.92) * mm, "end": v(271.4, 25.4) * mm});
            skLineSegment(sketch, "E131", {"start": v(203, 26.92) * mm, "end": v(203, 11.23) * mm});
            skLineSegment(sketch, "E132", {"start": v(203, 11.23) * mm, "end": v(271.4, 11.23) * mm});
            skLineSegment(sketch, "E133", {"start": v(271.4, 11.23) * mm, "end": v(271.4, 25.4) * mm});
            skSolve(sketch);
        }
        {
            var Q0;
            Q0 = qSketchRegion(id + "F19", true);
            extrude(context, id + "F20", {"entities" : qUnion([Q0]), "depth" : 1.27 * mm, "hasSecondDirection" : true, "secondDirectionOppositeDirection" : true, "secondDirectionDepth" : 1.27 * mm});
        }
        {
            var Q0;
            Q0=makeQuery(id+"F20.opExtrude","SWEPT_BODY",BODY,{"disambiguationData":[OSD([sQuery(id+"F19.wireOp",EDGE,"E130"),sQuery(id+"F19.wireOp",EDGE,"E131"),sQuery(id+"F19.wireOp",EDGE,"E132"),sQuery(id+"F19.wireOp",EDGE,"E133")])]});
            var Q1;
            Q1=makeQuery(id+"F1.opRevolve","SWEPT_EDGE",EDGE,{"disambiguationData":[OSD([sQuery(id+"F0.wireOp",EDGE,"E67"),sQuery(id+"F0.wireOp",EDGE,"E68")])]});
            circularPattern(context, id + "F21", {"operationType" : NewBodyOperationType.ADD, "entities" : qUnion([Q0]), "axis" : qUnion([Q1]), "angle" : 30 * degree, "instanceCount" : 16});
        }
        {
            var Q0;
            Q0=qCreatedBy(makeId("Top.planeOp"),FACE);
            var sketch = newSketch(context, id + "F22", { "sketchPlane" : qUnion([Q0])});
            skLineSegment(sketch, "E134", {"start": v(0, 0) * mm, "end": v(0, 102.87) * mm, "construction": true});
            skCircle(sketch, "E135", {"center": v(0, 102.87) * mm, "radius": 5.4 * mm});
            skSolve(sketch);
        }
        {
            var Q0;
            Q0 = qSketchRegion(id + "F22", true);
            extrude(context, id + "F23", {"entities" : qUnion([Q0]), "operationType" : NewBodyOperationType.ADD, "depth" : 26.67 * mm});
        }
        {
            var Q0;
            Q0=makeQuery(id+"F23.opExtrude","CAP_FACE",FACE,{"disambiguationData":[OSD([sQuery(id+"F22.wireOp",EDGE,"E135")])],"isStart":false});
            var sketch = newSketch(context, id + "F24", { "sketchPlane" : qUnion([Q0])});
            skCircle(sketch, "E136.cCircle", {"center": v(0, 102.87) * mm, "radius": 3.5 * mm, "construction": true});
            skLineSegment(sketch, "E136.0", {"start": v(3.5, 104.89) * mm, "end": v(3.5, 100.85) * mm});
            skLineSegment(sketch, "E136.1", {"start": v(3.5, 100.85) * mm, "end": v(0, 98.84) * mm});
            skLineSegment(sketch, "E136.2", {"start": v(0, 98.84) * mm, "end": v(-3.5, 100.85) * mm});
            skLineSegment(sketch, "E136.3", {"start": v(-3.5, 100.85) * mm, "end": v(-3.5, 104.89) * mm});
            skLineSegment(sketch, "E136.4", {"start": v(-3.5, 104.89) * mm, "end": v(0, 106.9) * mm});
            skLineSegment(sketch, "E136.5", {"start": v(0, 106.9) * mm, "end": v(3.5, 104.89) * mm});
            skPoint(sketch, "E136.0.midPoint", {"position": v(3.5, 102.87) * mm});
            skSolve(sketch);
        }
        {
            var Q0;
            Q0 = qSketchRegion(id + "F24", true);
            extrude(context, id + "F25", {"entities" : qUnion([Q0]), "operationType" : NewBodyOperationType.ADD, "depth" : 1.27 * mm});
        }
        {
            var Q0;
            Q0=makeQuery(id+"F1.opRevolve","SWEPT_FACE",FACE,{"disambiguationData":[OSD([sQuery(id+"F0.wireOp",EDGE,"E20.right")])]});
            var sketch = newSketch(context, id + "F26", { "sketchPlane" : qUnion([Q0])});
            skLineSegment(sketch, "E137", {"start": v(0, 6.6) * mm, "end": v(0, 17.15) * mm});
            skCircle(sketch, "E138", {"center": v(0, 11.87) * mm, "radius": 2.22 * mm});
            skCircle(sketch, "E139.1.0", {"center": v(-8.4, 8.4) * mm, "radius": 2.22 * mm});
            skCircle(sketch, "E139.2.0", {"center": v(-11.87, 0) * mm, "radius": 2.22 * mm});
            skCircle(sketch, "E139.3.0", {"center": v(-8.4, -8.4) * mm, "radius": 2.22 * mm});
            skCircle(sketch, "E139.4.0", {"center": v(0, -11.87) * mm, "radius": 2.22 * mm});
            skCircle(sketch, "E139.5.0", {"center": v(8.4, -8.4) * mm, "radius": 2.22 * mm});
            skCircle(sketch, "E139.6.0", {"center": v(11.87, 0) * mm, "radius": 2.22 * mm});
            skCircle(sketch, "E139.7.0", {"center": v(8.4, 8.4) * mm, "radius": 2.22 * mm});
            skPoint(sketch, "E139.center", {"position": v(0, 0) * mm});
            skSolve(sketch);
        }
        {
            var Q0;
            Q0 = qSketchRegion(id + "F26", true);
            extrude(context, id + "F27", {"entities" : qUnion([Q0]), "operationType" : NewBodyOperationType.REMOVE, "oppositeDirection" : true, "depth" : 2.54 * mm});
        }
        {
            var Q0;
            Q0=qCreatedBy(makeId("Front.planeOp"),FACE);
            cPlane(context, id + "F28", {"entities" : qUnion([Q0]), "cplaneType" : CPlaneType.OFFSET, "offset" : 12.7 * mm, "oppositeDirection" : true, "width" : 152.4 * mm, "height" : 152.4 * mm});
        }
        {
            var Q0;
            Q0=qCreatedBy(id+"F28.planeOp",FACE);
            var sketch = newSketch(context, id + "F29", { "sketchPlane" : qUnion([Q0])});
            skArc(sketch, "E140", {"start": v(-13.48, 19.25) * mm, "mid": v(-16.61, 16.61) * mm, "end": v(-19.25, 13.48) * mm});
            skArc(sketch, "E141", {"start": v(-16.43, 23.47) * mm, "mid": v(-20.26, 20.26) * mm, "end": v(-23.47, 16.43) * mm});
            skLineSegment(sketch, "E142", {"start": v(0, 0) * mm, "end": v(0, 28.65) * mm, "construction": true});
            skLineSegment(sketch, "E143", {"start": v(4.97, 28.21) * mm, "end": v(4.08, 23.14) * mm});
            skLineSegment(sketch, "E144", {"start": v(-4.08, 23.14) * mm, "end": v(-4.97, 28.21) * mm});
            skLineSegment(sketch, "E145.1.0", {"start": v(-19.25, 13.48) * mm, "end": v(-23.47, 16.43) * mm});
            skLineSegment(sketch, "E145.1.1", {"start": v(-16.43, 23.47) * mm, "end": v(-13.48, 19.25) * mm});
            skLineSegment(sketch, "E145.2.0", {"start": v(-23.14, -4.08) * mm, "end": v(-28.21, -4.97) * mm});
            skLineSegment(sketch, "E145.2.1", {"start": v(-28.21, 4.97) * mm, "end": v(-23.14, 4.08) * mm});
            skLineSegment(sketch, "E145.3.0", {"start": v(-13.48, -19.25) * mm, "end": v(-16.43, -23.47) * mm});
            skLineSegment(sketch, "E145.3.1", {"start": v(-23.47, -16.43) * mm, "end": v(-19.25, -13.48) * mm});
            skLineSegment(sketch, "E145.4.0", {"start": v(4.08, -23.14) * mm, "end": v(4.97, -28.21) * mm});
            skLineSegment(sketch, "E145.4.1", {"start": v(-4.97, -28.21) * mm, "end": v(-4.08, -23.14) * mm});
            skLineSegment(sketch, "E145.5.0", {"start": v(19.25, -13.48) * mm, "end": v(23.47, -16.43) * mm});
            skLineSegment(sketch, "E145.5.1", {"start": v(16.43, -23.47) * mm, "end": v(13.48, -19.25) * mm});
            skLineSegment(sketch, "E145.6.0", {"start": v(23.14, 4.08) * mm, "end": v(28.21, 4.97) * mm});
            skLineSegment(sketch, "E145.6.1", {"start": v(28.21, -4.97) * mm, "end": v(23.14, -4.08) * mm});
            skLineSegment(sketch, "E145.7.0", {"start": v(13.48, 19.25) * mm, "end": v(16.43, 23.47) * mm});
            skLineSegment(sketch, "E145.7.1", {"start": v(23.47, 16.43) * mm, "end": v(19.25, 13.48) * mm});
            skArc(sketch, "E146.trimOffspring", {"start": v(4.97, 28.21) * mm, "mid": v(0, 28.65) * mm, "end": v(-4.97, 28.21) * mm});
            skArc(sketch, "E147.trimOffspring", {"start": v(4.08, 23.14) * mm, "mid": v(0, 23.5) * mm, "end": v(-4.08, 23.14) * mm});
            skArc(sketch, "E148.trimOffspring", {"start": v(23.47, 16.43) * mm, "mid": v(20.26, 20.26) * mm, "end": v(16.43, 23.47) * mm});
            skArc(sketch, "E149.trimOffspring", {"start": v(19.25, 13.48) * mm, "mid": v(16.61, 16.61) * mm, "end": v(13.48, 19.25) * mm});
            skArc(sketch, "E150.trimOffspring", {"start": v(28.21, -4.97) * mm, "mid": v(28.65, 0) * mm, "end": v(28.21, 4.97) * mm});
            skArc(sketch, "E151.trimOffspring", {"start": v(23.14, -4.08) * mm, "mid": v(23.5, 0) * mm, "end": v(23.14, 4.08) * mm});
            skArc(sketch, "E152.trimOffspring", {"start": v(16.43, -23.47) * mm, "mid": v(20.26, -20.26) * mm, "end": v(23.47, -16.43) * mm});
            skArc(sketch, "E153.trimOffspring", {"start": v(13.48, -19.25) * mm, "mid": v(16.61, -16.61) * mm, "end": v(19.25, -13.48) * mm});
            skArc(sketch, "E154.trimOffspring", {"start": v(-4.97, -28.21) * mm, "mid": v(0, -28.65) * mm, "end": v(4.97, -28.21) * mm});
            skArc(sketch, "E155.trimOffspring", {"start": v(-4.08, -23.14) * mm, "mid": v(0, -23.5) * mm, "end": v(4.08, -23.14) * mm});
            skArc(sketch, "E156.trimOffspring", {"start": v(-23.47, -16.43) * mm, "mid": v(-20.26, -20.26) * mm, "end": v(-16.43, -23.47) * mm});
            skArc(sketch, "E157.trimOffspring", {"start": v(-19.25, -13.48) * mm, "mid": v(-16.61, -16.61) * mm, "end": v(-13.48, -19.25) * mm});
            skArc(sketch, "E158.trimOffspring", {"start": v(-28.21, 4.97) * mm, "mid": v(-28.65, 0) * mm, "end": v(-28.21, -4.97) * mm});
            skArc(sketch, "E159.trimOffspring", {"start": v(-23.14, 4.08) * mm, "mid": v(-23.5, 0) * mm, "end": v(-23.14, -4.08) * mm});
            skSolve(sketch);
        }
        {
            var Q0;
            Q0 = qSketchRegion(id + "F29", true);
            extrude(context, id + "F30", {"entities" : qUnion([Q0]), "operationType" : NewBodyOperationType.REMOVE, "oppositeDirection" : true, "depth" : 1.9 * mm, "hasSecondDirection" : true, "secondDirectionOppositeDirection" : false, "secondDirectionDepth" : 1.9 * mm});
        }
        {
            var Q0;
            Q0=makeQuery(id+"F1.opRevolve","SWEPT_FACE",FACE,{"disambiguationData":[OSD([sQuery(id+"F0.wireOp",EDGE,"E71")])]});
            var sketch = newSketch(context, id + "F31", { "sketchPlane" : qUnion([Q0])});
            skLineSegment(sketch, "E160", {"start": v(0, 0) * mm, "end": v(0, 27.02) * mm, "construction": true});
            skCircle(sketch, "E161", {"center": v(0, 28.93) * mm, "radius": 3.18 * mm});
            skCircle(sketch, "E162.1.0", {"center": v(-8.94, 27.51) * mm, "radius": 3.18 * mm});
            skCircle(sketch, "E162.2.0", {"center": v(-17, 23.4) * mm, "radius": 3.18 * mm});
            skCircle(sketch, "E162.3.0", {"center": v(-23.4, 17) * mm, "radius": 3.18 * mm});
            skCircle(sketch, "E162.4.0", {"center": v(-27.51, 8.94) * mm, "radius": 3.18 * mm});
            skCircle(sketch, "E162.5.0", {"center": v(-28.93, 0) * mm, "radius": 3.18 * mm});
            skCircle(sketch, "E162.6.0", {"center": v(-27.51, -8.94) * mm, "radius": 3.18 * mm});
            skCircle(sketch, "E162.7.0", {"center": v(-23.4, -17) * mm, "radius": 3.17 * mm});
            skCircle(sketch, "E162.8.0", {"center": v(-17, -23.4) * mm, "radius": 3.18 * mm});
            skCircle(sketch, "E162.9.0", {"center": v(-8.94, -27.51) * mm, "radius": 3.18 * mm});
            skCircle(sketch, "E162.10.0", {"center": v(0, -28.93) * mm, "radius": 3.18 * mm});
            skCircle(sketch, "E162.11.0", {"center": v(8.94, -27.51) * mm, "radius": 3.18 * mm});
            skCircle(sketch, "E162.12.0", {"center": v(17, -23.4) * mm, "radius": 3.18 * mm});
            skCircle(sketch, "E162.13.0", {"center": v(23.4, -17) * mm, "radius": 3.18 * mm});
            skCircle(sketch, "E162.14.0", {"center": v(27.51, -8.94) * mm, "radius": 3.18 * mm});
            skCircle(sketch, "E162.15.0", {"center": v(28.93, 0) * mm, "radius": 3.18 * mm});
            skCircle(sketch, "E162.16.0", {"center": v(27.51, 8.94) * mm, "radius": 3.18 * mm});
            skCircle(sketch, "E162.17.0", {"center": v(23.4, 17) * mm, "radius": 3.18 * mm});
            skCircle(sketch, "E162.18.0", {"center": v(17, 23.4) * mm, "radius": 3.18 * mm});
            skCircle(sketch, "E162.19.0", {"center": v(8.94, 27.51) * mm, "radius": 3.18 * mm});
            skPoint(sketch, "E162.center", {"position": v(0, 0) * mm});
            skSolve(sketch);
        }
        {
            var Q0;
            Q0 = qSketchRegion(id + "F31", true);
            extrude(context, id + "F32", {"entities" : qUnion([Q0]), "operationType" : NewBodyOperationType.REMOVE, "oppositeDirection" : true, "depth" : 5.08 * mm});
        }
        {
            var Q0;
            Q0=makeQuery(id+"F1.opRevolve","SWEPT_FACE",FACE,{"disambiguationData":[OSD([sQuery(id+"F0.wireOp",EDGE,"E23.trimOffspring")])]});
            var sketch = newSketch(context, id + "F33", { "sketchPlane" : qUnion([Q0])});
            skArc(sketch, "E163", {"start": v(-4.95, 17.26) * mm, "mid": v(-5.55, 17.08) * mm, "end": v(-6.14, 16.87) * mm});
            skArc(sketch, "E164", {"start": v(-5.43, 18.92) * mm, "mid": v(-6.08, 18.72) * mm, "end": v(-6.73, 18.5) * mm});
            skLineSegment(sketch, "E165", {"start": v(0, 0) * mm, "end": v(0, 19.69) * mm, "construction": true});
            skLineSegment(sketch, "E166", {"start": v(-0.69, 19.67) * mm, "end": v(-0.63, 17.94) * mm});
            skLineSegment(sketch, "E167", {"start": v(0.63, 17.94) * mm, "end": v(0.69, 19.67) * mm});
            skLineSegment(sketch, "E168.1.0", {"start": v(-6.73, 18.5) * mm, "end": v(-6.14, 16.87) * mm});
            skLineSegment(sketch, "E168.1.1", {"start": v(-4.95, 17.26) * mm, "end": v(-5.43, 18.92) * mm});
            skLineSegment(sketch, "E168.2.0", {"start": v(-12.12, 15.51) * mm, "end": v(-11.05, 14.15) * mm});
            skLineSegment(sketch, "E168.2.1", {"start": v(-10.04, 14.89) * mm, "end": v(-11, 16.32) * mm});
            skLineSegment(sketch, "E168.3.0", {"start": v(-16.32, 11) * mm, "end": v(-14.89, 10.04) * mm});
            skLineSegment(sketch, "E168.3.1", {"start": v(-14.15, 11.05) * mm, "end": v(-15.51, 12.12) * mm});
            skLineSegment(sketch, "E168.4.0", {"start": v(-18.92, 5.43) * mm, "end": v(-17.26, 4.95) * mm});
            skLineSegment(sketch, "E168.4.1", {"start": v(-16.87, 6.14) * mm, "end": v(-18.5, 6.73) * mm});
            skLineSegment(sketch, "E168.5.0", {"start": v(-19.67, -0.69) * mm, "end": v(-17.94, -0.63) * mm});
            skLineSegment(sketch, "E168.5.1", {"start": v(-17.94, 0.63) * mm, "end": v(-19.67, 0.69) * mm});
            skLineSegment(sketch, "E168.6.0", {"start": v(-18.5, -6.73) * mm, "end": v(-16.87, -6.14) * mm});
            skLineSegment(sketch, "E168.6.1", {"start": v(-17.26, -4.95) * mm, "end": v(-18.92, -5.43) * mm});
            skLineSegment(sketch, "E168.7.0", {"start": v(-15.51, -12.12) * mm, "end": v(-14.15, -11.05) * mm});
            skLineSegment(sketch, "E168.7.1", {"start": v(-14.89, -10.04) * mm, "end": v(-16.32, -11) * mm});
            skLineSegment(sketch, "E168.8.0", {"start": v(-11, -16.32) * mm, "end": v(-10.04, -14.89) * mm});
            skLineSegment(sketch, "E168.8.1", {"start": v(-11.05, -14.15) * mm, "end": v(-12.12, -15.51) * mm});
            skLineSegment(sketch, "E168.9.0", {"start": v(-5.43, -18.92) * mm, "end": v(-4.95, -17.26) * mm});
            skLineSegment(sketch, "E168.9.1", {"start": v(-6.14, -16.87) * mm, "end": v(-6.73, -18.5) * mm});
            skLineSegment(sketch, "E168.10.0", {"start": v(0.69, -19.67) * mm, "end": v(0.63, -17.94) * mm});
            skLineSegment(sketch, "E168.10.1", {"start": v(-0.63, -17.94) * mm, "end": v(-0.69, -19.67) * mm});
            skLineSegment(sketch, "E168.11.0", {"start": v(6.73, -18.5) * mm, "end": v(6.14, -16.87) * mm});
            skLineSegment(sketch, "E168.11.1", {"start": v(4.95, -17.26) * mm, "end": v(5.43, -18.92) * mm});
            skLineSegment(sketch, "E168.12.0", {"start": v(12.12, -15.51) * mm, "end": v(11.05, -14.15) * mm});
            skLineSegment(sketch, "E168.12.1", {"start": v(10.04, -14.89) * mm, "end": v(11, -16.32) * mm});
            skLineSegment(sketch, "E168.13.0", {"start": v(16.32, -11) * mm, "end": v(14.89, -10.04) * mm});
            skLineSegment(sketch, "E168.13.1", {"start": v(14.15, -11.05) * mm, "end": v(15.51, -12.12) * mm});
            skLineSegment(sketch, "E168.14.0", {"start": v(18.92, -5.43) * mm, "end": v(17.26, -4.95) * mm});
            skLineSegment(sketch, "E168.14.1", {"start": v(16.87, -6.14) * mm, "end": v(18.5, -6.73) * mm});
            skLineSegment(sketch, "E168.15.0", {"start": v(19.67, 0.69) * mm, "end": v(17.94, 0.63) * mm});
            skLineSegment(sketch, "E168.15.1", {"start": v(17.94, -0.63) * mm, "end": v(19.67, -0.69) * mm});
            skLineSegment(sketch, "E168.16.0", {"start": v(18.5, 6.73) * mm, "end": v(16.87, 6.14) * mm});
            skLineSegment(sketch, "E168.16.1", {"start": v(17.26, 4.95) * mm, "end": v(18.92, 5.43) * mm});
            skLineSegment(sketch, "E168.17.0", {"start": v(15.51, 12.12) * mm, "end": v(14.15, 11.05) * mm});
            skLineSegment(sketch, "E168.17.1", {"start": v(14.89, 10.04) * mm, "end": v(16.32, 11) * mm});
            skLineSegment(sketch, "E168.18.0", {"start": v(11, 16.32) * mm, "end": v(10.04, 14.89) * mm});
            skLineSegment(sketch, "E168.18.1", {"start": v(11.05, 14.15) * mm, "end": v(12.12, 15.51) * mm});
            skLineSegment(sketch, "E168.19.0", {"start": v(5.43, 18.92) * mm, "end": v(4.95, 17.26) * mm});
            skLineSegment(sketch, "E168.19.1", {"start": v(6.14, 16.87) * mm, "end": v(6.73, 18.5) * mm});
            skArc(sketch, "E169.trimOffspring", {"start": v(0.69, 19.67) * mm, "mid": v(0, 19.69) * mm, "end": v(-0.69, 19.67) * mm});
            skArc(sketch, "E170.trimOffspring", {"start": v(0.63, 17.94) * mm, "mid": v(0, 17.96) * mm, "end": v(-0.63, 17.94) * mm});
            skArc(sketch, "E171.trimOffspring", {"start": v(6.73, 18.5) * mm, "mid": v(6.08, 18.72) * mm, "end": v(5.43, 18.92) * mm});
            skArc(sketch, "E172.trimOffspring", {"start": v(6.14, 16.87) * mm, "mid": v(5.55, 17.08) * mm, "end": v(4.95, 17.26) * mm});
            skArc(sketch, "E173.trimOffspring", {"start": v(12.12, 15.51) * mm, "mid": v(11.57, 15.93) * mm, "end": v(11, 16.32) * mm});
            skArc(sketch, "E174.trimOffspring", {"start": v(11.05, 14.15) * mm, "mid": v(10.55, 14.53) * mm, "end": v(10.04, 14.89) * mm});
            skArc(sketch, "E175.trimOffspring", {"start": v(16.32, 11) * mm, "mid": v(15.93, 11.57) * mm, "end": v(15.51, 12.12) * mm});
            skArc(sketch, "E176.trimOffspring", {"start": v(14.89, 10.04) * mm, "mid": v(14.53, 10.55) * mm, "end": v(14.15, 11.05) * mm});
            skArc(sketch, "E177.trimOffspring", {"start": v(18.92, 5.43) * mm, "mid": v(18.72, 6.08) * mm, "end": v(18.5, 6.73) * mm});
            skArc(sketch, "E178.trimOffspring", {"start": v(17.26, 4.95) * mm, "mid": v(17.08, 5.55) * mm, "end": v(16.87, 6.14) * mm});
            skArc(sketch, "E179.trimOffspring", {"start": v(19.67, -0.69) * mm, "mid": v(19.69, 0) * mm, "end": v(19.67, 0.69) * mm});
            skArc(sketch, "E180.trimOffspring", {"start": v(17.94, -0.63) * mm, "mid": v(17.96, 0) * mm, "end": v(17.94, 0.63) * mm});
            skArc(sketch, "E181.trimOffspring", {"start": v(18.5, -6.73) * mm, "mid": v(18.72, -6.08) * mm, "end": v(18.92, -5.43) * mm});
            skArc(sketch, "E182.trimOffspring", {"start": v(16.87, -6.14) * mm, "mid": v(17.08, -5.55) * mm, "end": v(17.26, -4.95) * mm});
            skArc(sketch, "E183.trimOffspring", {"start": v(15.51, -12.12) * mm, "mid": v(15.93, -11.57) * mm, "end": v(16.32, -11) * mm});
            skArc(sketch, "E184.trimOffspring", {"start": v(14.15, -11.05) * mm, "mid": v(14.53, -10.55) * mm, "end": v(14.89, -10.04) * mm});
            skArc(sketch, "E185.trimOffspring", {"start": v(11, -16.32) * mm, "mid": v(11.57, -15.93) * mm, "end": v(12.12, -15.51) * mm});
            skArc(sketch, "E186.trimOffspring", {"start": v(10.04, -14.89) * mm, "mid": v(10.55, -14.53) * mm, "end": v(11.05, -14.15) * mm});
            skArc(sketch, "E187.trimOffspring", {"start": v(5.43, -18.92) * mm, "mid": v(6.08, -18.72) * mm, "end": v(6.73, -18.5) * mm});
            skArc(sketch, "E188.trimOffspring", {"start": v(4.95, -17.26) * mm, "mid": v(5.55, -17.08) * mm, "end": v(6.14, -16.87) * mm});
            skArc(sketch, "E189.trimOffspring", {"start": v(-0.69, -19.67) * mm, "mid": v(0, -19.69) * mm, "end": v(0.69, -19.67) * mm});
            skArc(sketch, "E190.trimOffspring", {"start": v(-0.63, -17.94) * mm, "mid": v(0, -17.96) * mm, "end": v(0.63, -17.94) * mm});
            skArc(sketch, "E191.trimOffspring", {"start": v(-6.73, -18.5) * mm, "mid": v(-6.08, -18.72) * mm, "end": v(-5.43, -18.92) * mm});
            skArc(sketch, "E192.trimOffspring", {"start": v(-6.14, -16.87) * mm, "mid": v(-5.55, -17.08) * mm, "end": v(-4.95, -17.26) * mm});
            skArc(sketch, "E193.trimOffspring", {"start": v(-12.12, -15.51) * mm, "mid": v(-11.57, -15.93) * mm, "end": v(-11, -16.32) * mm});
            skArc(sketch, "E194.trimOffspring", {"start": v(-11.05, -14.15) * mm, "mid": v(-10.55, -14.53) * mm, "end": v(-10.04, -14.89) * mm});
            skArc(sketch, "E195.trimOffspring", {"start": v(-16.32, -11) * mm, "mid": v(-15.93, -11.57) * mm, "end": v(-15.51, -12.12) * mm});
            skArc(sketch, "E196.trimOffspring", {"start": v(-14.89, -10.04) * mm, "mid": v(-14.53, -10.55) * mm, "end": v(-14.15, -11.05) * mm});
            skArc(sketch, "E197.trimOffspring", {"start": v(-18.92, -5.43) * mm, "mid": v(-18.72, -6.08) * mm, "end": v(-18.5, -6.73) * mm});
            skArc(sketch, "E198.trimOffspring", {"start": v(-17.26, -4.95) * mm, "mid": v(-17.08, -5.55) * mm, "end": v(-16.87, -6.14) * mm});
            skArc(sketch, "E199.trimOffspring", {"start": v(-19.67, 0.69) * mm, "mid": v(-19.69, 0) * mm, "end": v(-19.67, -0.69) * mm});
            skArc(sketch, "E200.trimOffspring", {"start": v(-17.94, 0.63) * mm, "mid": v(-17.96, 0) * mm, "end": v(-17.94, -0.63) * mm});
            skArc(sketch, "E201.trimOffspring", {"start": v(-18.5, 6.73) * mm, "mid": v(-18.72, 6.08) * mm, "end": v(-18.92, 5.43) * mm});
            skArc(sketch, "E202.trimOffspring", {"start": v(-16.87, 6.14) * mm, "mid": v(-17.08, 5.55) * mm, "end": v(-17.26, 4.95) * mm});
            skArc(sketch, "E203.trimOffspring", {"start": v(-15.51, 12.12) * mm, "mid": v(-15.93, 11.57) * mm, "end": v(-16.32, 11) * mm});
            skArc(sketch, "E204.trimOffspring", {"start": v(-14.15, 11.05) * mm, "mid": v(-14.53, 10.55) * mm, "end": v(-14.89, 10.04) * mm});
            skArc(sketch, "E205.trimOffspring", {"start": v(-11, 16.32) * mm, "mid": v(-11.57, 15.93) * mm, "end": v(-12.12, 15.51) * mm});
            skArc(sketch, "E206.trimOffspring", {"start": v(-10.04, 14.89) * mm, "mid": v(-10.55, 14.53) * mm, "end": v(-11.05, 14.15) * mm});
            skSolve(sketch);
        }
        {
            var Q0;
            Q0 = qSketchRegion(id + "F33", true);
            extrude(context, id + "F34", {"entities" : qUnion([Q0]), "operationType" : NewBodyOperationType.REMOVE, "depth" : 25.4 * mm});
        }
        {
            var Q0;
            Q0=makeQuery(id+"F30.boolean.opBoolean","COPY",EDGE,{"derivedFrom":makeQuery(id+"F30.opExtrude","CAP_EDGE",EDGE,{"disambiguationData":[OSD([sQuery(id+"F29.wireOp",EDGE,"E145.7.0")])],"isStart":false})});
            var Q1;
            Q1=makeQuery(id+"F30.boolean.opBoolean","COPY",EDGE,{"derivedFrom":makeQuery(id+"F30.opExtrude","CAP_EDGE",EDGE,{"disambiguationData":[OSD([sQuery(id+"F29.wireOp",EDGE,"E145.7.0")])],"isStart":true})});
            var Q2;
            Q2=makeQuery(id+"F30.boolean.opBoolean","COPY",EDGE,{"derivedFrom":makeQuery(id+"F30.opExtrude","CAP_EDGE",EDGE,{"disambiguationData":[OSD([sQuery(id+"F29.wireOp",EDGE,"E144")])],"isStart":true})});
            var Q3;
            Q3=makeQuery(id+"F30.boolean.opBoolean","COPY",EDGE,{"derivedFrom":makeQuery(id+"F30.opExtrude","CAP_EDGE",EDGE,{"disambiguationData":[OSD([sQuery(id+"F29.wireOp",EDGE,"E144")])],"isStart":false})});
            var Q4;
            Q4=makeQuery(id+"F30.boolean.opBoolean","COPY",EDGE,{"derivedFrom":makeQuery(id+"F30.opExtrude","CAP_EDGE",EDGE,{"disambiguationData":[OSD([sQuery(id+"F29.wireOp",EDGE,"E145.7.1")])],"isStart":true})});
            var Q5;
            Q5=makeQuery(id+"F30.boolean.opBoolean","COPY",EDGE,{"derivedFrom":makeQuery(id+"F30.opExtrude","CAP_EDGE",EDGE,{"disambiguationData":[OSD([sQuery(id+"F29.wireOp",EDGE,"E143")])],"isStart":true})});
            var Q6;
            Q6=makeQuery(id+"F30.boolean.opBoolean","COPY",EDGE,{"derivedFrom":makeQuery(id+"F30.opExtrude","CAP_EDGE",EDGE,{"disambiguationData":[OSD([sQuery(id+"F29.wireOp",EDGE,"E145.7.1")])],"isStart":false})});
            var Q7;
            Q7=makeQuery(id+"F30.boolean.opBoolean","COPY",EDGE,{"derivedFrom":makeQuery(id+"F30.opExtrude","CAP_EDGE",EDGE,{"disambiguationData":[OSD([sQuery(id+"F29.wireOp",EDGE,"E143")])],"isStart":false})});
            var Q8;
            Q8=makeQuery(id+"F30.boolean.opBoolean","COPY",EDGE,{"derivedFrom":makeQuery(id+"F30.opExtrude","CAP_EDGE",EDGE,{"disambiguationData":[OSD([sQuery(id+"F29.wireOp",EDGE,"E145.6.1")])],"isStart":false})});
            var Q9;
            Q9=makeQuery(id+"F30.boolean.opBoolean","COPY",EDGE,{"derivedFrom":makeQuery(id+"F30.opExtrude","CAP_EDGE",EDGE,{"disambiguationData":[OSD([sQuery(id+"F29.wireOp",EDGE,"E145.6.1")])],"isStart":true})});
            var Q10;
            Q10=makeQuery(id+"F30.boolean.opBoolean","COPY",EDGE,{"derivedFrom":makeQuery(id+"F30.opExtrude","CAP_EDGE",EDGE,{"disambiguationData":[OSD([sQuery(id+"F29.wireOp",EDGE,"E145.6.0")])],"isStart":true})});
            var Q11;
            Q11=makeQuery(id+"F30.boolean.opBoolean","COPY",EDGE,{"derivedFrom":makeQuery(id+"F30.opExtrude","CAP_EDGE",EDGE,{"disambiguationData":[OSD([sQuery(id+"F29.wireOp",EDGE,"E145.6.0")])],"isStart":false})});
            var Q12;
            Q12=makeQuery(id+"F30.boolean.opBoolean","COPY",EDGE,{"derivedFrom":makeQuery(id+"F30.opExtrude","CAP_EDGE",EDGE,{"disambiguationData":[OSD([sQuery(id+"F29.wireOp",EDGE,"E145.5.1")])],"isStart":false})});
            var Q13;
            Q13=makeQuery(id+"F30.boolean.opBoolean","COPY",EDGE,{"derivedFrom":makeQuery(id+"F30.opExtrude","CAP_EDGE",EDGE,{"disambiguationData":[OSD([sQuery(id+"F29.wireOp",EDGE,"E145.5.0")])],"isStart":false})});
            var Q14;
            Q14=makeQuery(id+"F30.boolean.opBoolean","COPY",EDGE,{"derivedFrom":makeQuery(id+"F30.opExtrude","CAP_EDGE",EDGE,{"disambiguationData":[OSD([sQuery(id+"F29.wireOp",EDGE,"E145.5.1")])],"isStart":true})});
            var Q15;
            Q15=makeQuery(id+"F30.boolean.opBoolean","COPY",EDGE,{"derivedFrom":makeQuery(id+"F30.opExtrude","CAP_EDGE",EDGE,{"disambiguationData":[OSD([sQuery(id+"F29.wireOp",EDGE,"E145.5.0")])],"isStart":true})});
            var Q16;
            Q16=makeQuery(id+"F30.boolean.opBoolean","COPY",EDGE,{"derivedFrom":makeQuery(id+"F30.opExtrude","CAP_EDGE",EDGE,{"disambiguationData":[OSD([sQuery(id+"F29.wireOp",EDGE,"E145.4.1")])],"isStart":true})});
            var Q17;
            Q17=makeQuery(id+"F30.boolean.opBoolean","COPY",EDGE,{"derivedFrom":makeQuery(id+"F30.opExtrude","CAP_EDGE",EDGE,{"disambiguationData":[OSD([sQuery(id+"F29.wireOp",EDGE,"E145.4.0")])],"isStart":true})});
            var Q18;
            Q18=makeQuery(id+"F30.boolean.opBoolean","COPY",EDGE,{"derivedFrom":makeQuery(id+"F30.opExtrude","CAP_EDGE",EDGE,{"disambiguationData":[OSD([sQuery(id+"F29.wireOp",EDGE,"E145.4.1")])],"isStart":false})});
            var Q19;
            Q19=makeQuery(id+"F30.boolean.opBoolean","COPY",EDGE,{"derivedFrom":makeQuery(id+"F30.opExtrude","CAP_EDGE",EDGE,{"disambiguationData":[OSD([sQuery(id+"F29.wireOp",EDGE,"E145.4.0")])],"isStart":false})});
            var Q20;
            Q20=makeQuery(id+"F30.boolean.opBoolean","COPY",EDGE,{"derivedFrom":makeQuery(id+"F30.opExtrude","CAP_EDGE",EDGE,{"disambiguationData":[OSD([sQuery(id+"F29.wireOp",EDGE,"E145.3.0")])],"isStart":false})});
            var Q21;
            Q21=makeQuery(id+"F30.boolean.opBoolean","COPY",EDGE,{"derivedFrom":makeQuery(id+"F30.opExtrude","CAP_EDGE",EDGE,{"disambiguationData":[OSD([sQuery(id+"F29.wireOp",EDGE,"E145.3.1")])],"isStart":false})});
            var Q22;
            Q22=makeQuery(id+"F30.boolean.opBoolean","COPY",EDGE,{"derivedFrom":makeQuery(id+"F30.opExtrude","CAP_EDGE",EDGE,{"disambiguationData":[OSD([sQuery(id+"F29.wireOp",EDGE,"E145.3.1")])],"isStart":true})});
            var Q23;
            Q23=makeQuery(id+"F30.boolean.opBoolean","COPY",EDGE,{"derivedFrom":makeQuery(id+"F30.opExtrude","CAP_EDGE",EDGE,{"disambiguationData":[OSD([sQuery(id+"F29.wireOp",EDGE,"E145.3.0")])],"isStart":true})});
            var Q24;
            Q24=makeQuery(id+"F30.boolean.opBoolean","COPY",EDGE,{"derivedFrom":makeQuery(id+"F30.opExtrude","CAP_EDGE",EDGE,{"disambiguationData":[OSD([sQuery(id+"F29.wireOp",EDGE,"E145.2.1")])],"isStart":false})});
            var Q25;
            Q25=makeQuery(id+"F30.boolean.opBoolean","COPY",EDGE,{"derivedFrom":makeQuery(id+"F30.opExtrude","CAP_EDGE",EDGE,{"disambiguationData":[OSD([sQuery(id+"F29.wireOp",EDGE,"E145.2.0")])],"isStart":false})});
            var Q26;
            Q26=makeQuery(id+"F30.boolean.opBoolean","COPY",EDGE,{"derivedFrom":makeQuery(id+"F30.opExtrude","CAP_EDGE",EDGE,{"disambiguationData":[OSD([sQuery(id+"F29.wireOp",EDGE,"E145.2.0")])],"isStart":true})});
            var Q27;
            Q27=makeQuery(id+"F30.boolean.opBoolean","COPY",EDGE,{"derivedFrom":makeQuery(id+"F30.opExtrude","CAP_EDGE",EDGE,{"disambiguationData":[OSD([sQuery(id+"F29.wireOp",EDGE,"E145.2.1")])],"isStart":true})});
            var Q28;
            Q28=makeQuery(id+"F30.boolean.opBoolean","COPY",EDGE,{"derivedFrom":makeQuery(id+"F30.opExtrude","CAP_EDGE",EDGE,{"disambiguationData":[OSD([sQuery(id+"F29.wireOp",EDGE,"E145.1.1")])],"isStart":true})});
            var Q29;
            Q29=makeQuery(id+"F30.boolean.opBoolean","COPY",EDGE,{"derivedFrom":makeQuery(id+"F30.opExtrude","CAP_EDGE",EDGE,{"disambiguationData":[OSD([sQuery(id+"F29.wireOp",EDGE,"E145.1.0")])],"isStart":true})});
            var Q30;
            Q30=makeQuery(id+"F30.boolean.opBoolean","COPY",EDGE,{"derivedFrom":makeQuery(id+"F30.opExtrude","CAP_EDGE",EDGE,{"disambiguationData":[OSD([sQuery(id+"F29.wireOp",EDGE,"E145.1.0")])],"isStart":false})});
            var Q31;
            Q31=makeQuery(id+"F30.boolean.opBoolean","COPY",EDGE,{"derivedFrom":makeQuery(id+"F30.opExtrude","CAP_EDGE",EDGE,{"disambiguationData":[OSD([sQuery(id+"F29.wireOp",EDGE,"E145.1.1")])],"isStart":false})});
            fillet(context, id + "F35", {"entities" : qUnion([Q0, Q1, Q2, Q3, Q4, Q5, Q6, Q7, Q8, Q9, Q10, Q11, Q12, Q13, Q14, Q15, Q16, Q17, Q18, Q19, Q20, Q21, Q22, Q23, Q24, Q25, Q26, Q27, Q28, Q29, Q30, Q31]), "radius" : 0.64 * mm, "tangentPropagation" : true, "allowEdgeOverflow" : false});
        }
        {
            var Q0;
            Q0=makeQuery(id+"F18.boolean.opBoolean","INTERSECT",EDGE,{"derivedFrom":[makeQuery(id+"F18.opPattern","COPY",FACE,{"derivedFrom":makeQuery(id+"F10.opSweep","SWEPT_FACE",FACE,{"disambiguationData":[OSD([sQuery(id+"F7.wireOp",EDGE,"E115"),sQuery(id+"F9.wireOp",EDGE,"E120")])]}),"instanceName":"2"}),makeQuery(id+"F18.opPattern","COPY",FACE,{"derivedFrom":makeQuery(id+"F12.opRevolve","SWEPT_FACE",FACE,{"disambiguationData":[OSD([sQuery(id+"F11.wireOp",EDGE,"E121.top")])]}),"instanceName":"2"})]});
            var Q1;
            Q1=makeQuery(id+"F18.boolean.opBoolean","INTERSECT",EDGE,{"derivedFrom":[makeQuery(id+"F18.opPattern","COPY",FACE,{"derivedFrom":makeQuery(id+"F10.opSweep","SWEPT_FACE",FACE,{"disambiguationData":[OSD([sQuery(id+"F7.wireOp",EDGE,"E115"),sQuery(id+"F9.wireOp",EDGE,"E120")])]}),"instanceName":"1"}),makeQuery(id+"F18.opPattern","COPY",FACE,{"derivedFrom":makeQuery(id+"F12.opRevolve","SWEPT_FACE",FACE,{"disambiguationData":[OSD([sQuery(id+"F11.wireOp",EDGE,"E121.top")])]}),"instanceName":"1"})]});
            var Q2;
            Q2=makeQuery(id+"F18.boolean.opBoolean","INTERSECT",EDGE,{"derivedFrom":[makeQuery(id+"F10.opSweep","SWEPT_FACE",FACE,{"disambiguationData":[OSD([sQuery(id+"F7.wireOp",EDGE,"E115"),sQuery(id+"F9.wireOp",EDGE,"E120")])]}),makeQuery(id+"F12.opRevolve","SWEPT_FACE",FACE,{"disambiguationData":[OSD([sQuery(id+"F11.wireOp",EDGE,"E121.top")])]})]});
            var Q3;
            Q3=makeQuery(id+"F18.boolean.opBoolean","INTERSECT",EDGE,{"derivedFrom":[makeQuery(id+"F18.opPattern","COPY",FACE,{"derivedFrom":makeQuery(id+"F10.opSweep","SWEPT_FACE",FACE,{"disambiguationData":[OSD([sQuery(id+"F7.wireOp",EDGE,"E115"),sQuery(id+"F9.wireOp",EDGE,"E120")])]}),"instanceName":"7"}),makeQuery(id+"F18.opPattern","COPY",FACE,{"derivedFrom":makeQuery(id+"F12.opRevolve","SWEPT_FACE",FACE,{"disambiguationData":[OSD([sQuery(id+"F11.wireOp",EDGE,"E121.top")])]}),"instanceName":"7"})]});
            var Q4;
            Q4=makeQuery(id+"F18.boolean.opBoolean","INTERSECT",EDGE,{"derivedFrom":[makeQuery(id+"F18.opPattern","COPY",FACE,{"derivedFrom":makeQuery(id+"F10.opSweep","SWEPT_FACE",FACE,{"disambiguationData":[OSD([sQuery(id+"F7.wireOp",EDGE,"E115"),sQuery(id+"F9.wireOp",EDGE,"E120")])]}),"instanceName":"6"}),makeQuery(id+"F18.opPattern","COPY",FACE,{"derivedFrom":makeQuery(id+"F12.opRevolve","SWEPT_FACE",FACE,{"disambiguationData":[OSD([sQuery(id+"F11.wireOp",EDGE,"E121.top")])]}),"instanceName":"6"})]});
            var Q5;
            Q5=makeQuery(id+"F18.boolean.opBoolean","INTERSECT",EDGE,{"derivedFrom":[makeQuery(id+"F18.opPattern","COPY",FACE,{"derivedFrom":makeQuery(id+"F10.opSweep","SWEPT_FACE",FACE,{"disambiguationData":[OSD([sQuery(id+"F7.wireOp",EDGE,"E115"),sQuery(id+"F9.wireOp",EDGE,"E120")])]}),"instanceName":"5"}),makeQuery(id+"F18.opPattern","COPY",FACE,{"derivedFrom":makeQuery(id+"F12.opRevolve","SWEPT_FACE",FACE,{"disambiguationData":[OSD([sQuery(id+"F11.wireOp",EDGE,"E121.top")])]}),"instanceName":"5"})]});
            var Q6;
            Q6=makeQuery(id+"F18.boolean.opBoolean","INTERSECT",EDGE,{"derivedFrom":[makeQuery(id+"F18.opPattern","COPY",FACE,{"derivedFrom":makeQuery(id+"F10.opSweep","SWEPT_FACE",FACE,{"disambiguationData":[OSD([sQuery(id+"F7.wireOp",EDGE,"E115"),sQuery(id+"F9.wireOp",EDGE,"E120")])]}),"instanceName":"4"}),makeQuery(id+"F18.opPattern","COPY",FACE,{"derivedFrom":makeQuery(id+"F12.opRevolve","SWEPT_FACE",FACE,{"disambiguationData":[OSD([sQuery(id+"F11.wireOp",EDGE,"E121.top")])]}),"instanceName":"4"})]});
            var Q7;
            Q7=makeQuery(id+"F18.boolean.opBoolean","INTERSECT",EDGE,{"derivedFrom":[makeQuery(id+"F18.opPattern","COPY",FACE,{"derivedFrom":makeQuery(id+"F10.opSweep","SWEPT_FACE",FACE,{"disambiguationData":[OSD([sQuery(id+"F7.wireOp",EDGE,"E115"),sQuery(id+"F9.wireOp",EDGE,"E120")])]}),"instanceName":"3"}),makeQuery(id+"F18.opPattern","COPY",FACE,{"derivedFrom":makeQuery(id+"F12.opRevolve","SWEPT_FACE",FACE,{"disambiguationData":[OSD([sQuery(id+"F11.wireOp",EDGE,"E121.top")])]}),"instanceName":"3"})]});
            fillet(context, id + "F36", {"entities" : qUnion([Q0, Q1, Q2, Q3, Q4, Q5, Q6, Q7]), "radius" : 1.27 * mm, "tangentPropagation" : true, "allowEdgeOverflow" : false});
        }
        {
            var Q0;
            Q0=makeQuery(id+"F18.boolean.opBoolean","INTERSECT",EDGE,{"derivedFrom":[makeQuery(id+"F18.opPattern","COPY",FACE,{"derivedFrom":makeQuery(id+"F10.opSweep","SWEPT_FACE",FACE,{"disambiguationData":[OSD([sQuery(id+"F7.wireOp",EDGE,"E117"),sQuery(id+"F9.wireOp",EDGE,"E120")])]}),"instanceName":"2"}),makeQuery(id+"F18.opPattern","COPY",FACE,{"derivedFrom":makeQuery(id+"F12.opRevolve","SWEPT_FACE",FACE,{"disambiguationData":[OSD([sQuery(id+"F11.wireOp",EDGE,"E122.top")])]}),"instanceName":"2"})]});
            var Q1;
            Q1=makeQuery(id+"F18.boolean.opBoolean","INTERSECT",EDGE,{"derivedFrom":[makeQuery(id+"F18.opPattern","COPY",FACE,{"derivedFrom":makeQuery(id+"F10.opSweep","SWEPT_FACE",FACE,{"disambiguationData":[OSD([sQuery(id+"F7.wireOp",EDGE,"E117"),sQuery(id+"F9.wireOp",EDGE,"E120")])]}),"instanceName":"1"}),makeQuery(id+"F18.opPattern","COPY",FACE,{"derivedFrom":makeQuery(id+"F12.opRevolve","SWEPT_FACE",FACE,{"disambiguationData":[OSD([sQuery(id+"F11.wireOp",EDGE,"E122.top")])]}),"instanceName":"1"})]});
            var Q2;
            Q2=makeQuery(id+"F18.boolean.opBoolean","INTERSECT",EDGE,{"derivedFrom":[makeQuery(id+"F10.opSweep","SWEPT_FACE",FACE,{"disambiguationData":[OSD([sQuery(id+"F7.wireOp",EDGE,"E117"),sQuery(id+"F9.wireOp",EDGE,"E120")])]}),makeQuery(id+"F12.opRevolve","SWEPT_FACE",FACE,{"disambiguationData":[OSD([sQuery(id+"F11.wireOp",EDGE,"E122.top")])]})]});
            var Q3;
            Q3=makeQuery(id+"F18.boolean.opBoolean","INTERSECT",EDGE,{"derivedFrom":[makeQuery(id+"F18.opPattern","COPY",FACE,{"derivedFrom":makeQuery(id+"F10.opSweep","SWEPT_FACE",FACE,{"disambiguationData":[OSD([sQuery(id+"F7.wireOp",EDGE,"E117"),sQuery(id+"F9.wireOp",EDGE,"E120")])]}),"instanceName":"7"}),makeQuery(id+"F18.opPattern","COPY",FACE,{"derivedFrom":makeQuery(id+"F12.opRevolve","SWEPT_FACE",FACE,{"disambiguationData":[OSD([sQuery(id+"F11.wireOp",EDGE,"E122.top")])]}),"instanceName":"7"})]});
            var Q4;
            Q4=makeQuery(id+"F18.boolean.opBoolean","INTERSECT",EDGE,{"derivedFrom":[makeQuery(id+"F18.opPattern","COPY",FACE,{"derivedFrom":makeQuery(id+"F10.opSweep","SWEPT_FACE",FACE,{"disambiguationData":[OSD([sQuery(id+"F7.wireOp",EDGE,"E117"),sQuery(id+"F9.wireOp",EDGE,"E120")])]}),"instanceName":"6"}),makeQuery(id+"F18.opPattern","COPY",FACE,{"derivedFrom":makeQuery(id+"F12.opRevolve","SWEPT_FACE",FACE,{"disambiguationData":[OSD([sQuery(id+"F11.wireOp",EDGE,"E122.top")])]}),"instanceName":"6"})]});
            var Q5;
            Q5=makeQuery(id+"F18.boolean.opBoolean","INTERSECT",EDGE,{"derivedFrom":[makeQuery(id+"F18.opPattern","COPY",FACE,{"derivedFrom":makeQuery(id+"F10.opSweep","SWEPT_FACE",FACE,{"disambiguationData":[OSD([sQuery(id+"F7.wireOp",EDGE,"E117"),sQuery(id+"F9.wireOp",EDGE,"E120")])]}),"instanceName":"5"}),makeQuery(id+"F18.opPattern","COPY",FACE,{"derivedFrom":makeQuery(id+"F12.opRevolve","SWEPT_FACE",FACE,{"disambiguationData":[OSD([sQuery(id+"F11.wireOp",EDGE,"E122.top")])]}),"instanceName":"5"})]});
            var Q6;
            Q6=makeQuery(id+"F18.boolean.opBoolean","INTERSECT",EDGE,{"derivedFrom":[makeQuery(id+"F18.opPattern","COPY",FACE,{"derivedFrom":makeQuery(id+"F10.opSweep","SWEPT_FACE",FACE,{"disambiguationData":[OSD([sQuery(id+"F7.wireOp",EDGE,"E117"),sQuery(id+"F9.wireOp",EDGE,"E120")])]}),"instanceName":"4"}),makeQuery(id+"F18.opPattern","COPY",FACE,{"derivedFrom":makeQuery(id+"F12.opRevolve","SWEPT_FACE",FACE,{"disambiguationData":[OSD([sQuery(id+"F11.wireOp",EDGE,"E122.top")])]}),"instanceName":"4"})]});
            var Q7;
            Q7=makeQuery(id+"F18.boolean.opBoolean","INTERSECT",EDGE,{"derivedFrom":[makeQuery(id+"F18.opPattern","COPY",FACE,{"derivedFrom":makeQuery(id+"F10.opSweep","SWEPT_FACE",FACE,{"disambiguationData":[OSD([sQuery(id+"F7.wireOp",EDGE,"E117"),sQuery(id+"F9.wireOp",EDGE,"E120")])]}),"instanceName":"3"}),makeQuery(id+"F18.opPattern","COPY",FACE,{"derivedFrom":makeQuery(id+"F12.opRevolve","SWEPT_FACE",FACE,{"disambiguationData":[OSD([sQuery(id+"F11.wireOp",EDGE,"E122.top")])]}),"instanceName":"3"})]});
            fillet(context, id + "F37", {"entities" : qUnion([Q0, Q1, Q2, Q3, Q4, Q5, Q6, Q7]), "radius" : 1.27 * mm, "tangentPropagation" : true, "allowEdgeOverflow" : false});
        }
        {
            var Q0;
            Q0=makeQuery(id+"F1.opRevolve","SWEPT_EDGE",EDGE,{"disambiguationData":[OSD([sQuery(id+"F0.wireOp",EDGE,"E9"),sQuery(id+"F0.wireOp",EDGE,"E60.trimOffspring")])]});
            fillet(context, id + "F38", {"entities" : qUnion([Q0]), "radius" : 6.35 * mm, "tangentPropagation" : true, "allowEdgeOverflow" : false});
        }
        {
            var Q0;
            Q0=makeQuery(id+"F1.opRevolve","SWEPT_EDGE",EDGE,{"disambiguationData":[OSD([sQuery(id+"F0.wireOp",EDGE,"E7"),sQuery(id+"F0.wireOp",EDGE,"E8")])]});
            chamfer(context, id + "F39", {"entities" : qUnion([Q0]), "width" : 0.64 * mm, "tangentPropagation" : true});
        }
        {
            var Q0;
            {var subQ0=sQuery(id+"F0.wireOp",EDGE,"E1");var subQ1=sQuery(id+"F0.wireOp",EDGE,"E67");var subQ2=sQuery(id+"F19.wireOp",EDGE,"E133");var subQ3=sQuery(id+"F19.wireOp",EDGE,"E132");var subQ4=sQuery(id+"F19.wireOp",EDGE,"E131");var subQ5=sQuery(id+"F19.wireOp",EDGE,"E130");Q0=makeQuery(id+"F21.boolean.opBoolean","SPLIT",EDGE,{"disambiguationData":[TD([makeQuery(id+"F21.opPattern","COPY",FACE,{"derivedFrom":makeQuery(id+"F20.opExtrude","CAP_FACE",FACE,{"disambiguationData":[OSD([subQ5,subQ4,subQ3,subQ2])],"isStart":true}),"instanceName":"10"})])],"derivedFrom":makeQuery(id+"F1.opRevolve","SWEPT_EDGE",EDGE,{"disambiguationData":[OSD([subQ0,subQ1])]})});}
            var Q1;
            {var subQ0=sQuery(id+"F0.wireOp",EDGE,"E1");var subQ1=sQuery(id+"F19.wireOp",EDGE,"E133");var subQ2=sQuery(id+"F19.wireOp",EDGE,"E132");var subQ3=sQuery(id+"F19.wireOp",EDGE,"E131");var subQ4=sQuery(id+"F19.wireOp",EDGE,"E130");var subQ5=sQuery(id+"F0.wireOp",EDGE,"E67");Q1=makeQuery(id+"F21.boolean.opBoolean","SPLIT",EDGE,{"disambiguationData":[TD([makeQuery(id+"F21.opPattern","COPY",FACE,{"derivedFrom":makeQuery(id+"F20.opExtrude","CAP_FACE",FACE,{"disambiguationData":[OSD([subQ4,subQ3,subQ2,subQ1])],"isStart":true}),"instanceName":"9"})])],"derivedFrom":makeQuery(id+"F1.opRevolve","SWEPT_EDGE",EDGE,{"disambiguationData":[OSD([subQ0,subQ5])]})});}
            var Q2;
            {var subQ0=sQuery(id+"F0.wireOp",EDGE,"E1");var subQ1=sQuery(id+"F0.wireOp",EDGE,"E67");var subQ2=sQuery(id+"F19.wireOp",EDGE,"E133");var subQ3=sQuery(id+"F19.wireOp",EDGE,"E132");var subQ4=sQuery(id+"F19.wireOp",EDGE,"E131");var subQ5=sQuery(id+"F19.wireOp",EDGE,"E130");Q2=makeQuery(id+"F21.boolean.opBoolean","SPLIT",EDGE,{"disambiguationData":[TD([makeQuery(id+"F21.opPattern","COPY",FACE,{"derivedFrom":makeQuery(id+"F20.opExtrude","CAP_FACE",FACE,{"disambiguationData":[OSD([subQ5,subQ4,subQ3,subQ2])],"isStart":true}),"instanceName":"8"})])],"derivedFrom":makeQuery(id+"F1.opRevolve","SWEPT_EDGE",EDGE,{"disambiguationData":[OSD([subQ0,subQ1])]})});}
            var Q3;
            {var subQ0=sQuery(id+"F0.wireOp",EDGE,"E1");var subQ1=sQuery(id+"F19.wireOp",EDGE,"E133");var subQ2=sQuery(id+"F19.wireOp",EDGE,"E132");var subQ3=sQuery(id+"F19.wireOp",EDGE,"E131");var subQ4=sQuery(id+"F19.wireOp",EDGE,"E130");var subQ5=sQuery(id+"F0.wireOp",EDGE,"E67");Q3=makeQuery(id+"F21.boolean.opBoolean","SPLIT",EDGE,{"disambiguationData":[TD([makeQuery(id+"F21.opPattern","COPY",FACE,{"derivedFrom":makeQuery(id+"F20.opExtrude","CAP_FACE",FACE,{"disambiguationData":[OSD([subQ4,subQ3,subQ2,subQ1])],"isStart":true}),"instanceName":"7"})])],"derivedFrom":makeQuery(id+"F1.opRevolve","SWEPT_EDGE",EDGE,{"disambiguationData":[OSD([subQ0,subQ5])]})});}
            var Q4;
            {var subQ0=sQuery(id+"F0.wireOp",EDGE,"E1");var subQ1=sQuery(id+"F0.wireOp",EDGE,"E67");var subQ2=sQuery(id+"F19.wireOp",EDGE,"E133");var subQ3=sQuery(id+"F19.wireOp",EDGE,"E132");var subQ4=sQuery(id+"F19.wireOp",EDGE,"E131");var subQ5=sQuery(id+"F19.wireOp",EDGE,"E130");Q4=makeQuery(id+"F21.boolean.opBoolean","SPLIT",EDGE,{"disambiguationData":[TD([makeQuery(id+"F21.opPattern","COPY",FACE,{"derivedFrom":makeQuery(id+"F20.opExtrude","CAP_FACE",FACE,{"disambiguationData":[OSD([subQ5,subQ4,subQ3,subQ2])],"isStart":true}),"instanceName":"6"})])],"derivedFrom":makeQuery(id+"F1.opRevolve","SWEPT_EDGE",EDGE,{"disambiguationData":[OSD([subQ0,subQ1])]})});}
            var Q5;
            {var subQ0=sQuery(id+"F0.wireOp",EDGE,"E1");var subQ1=sQuery(id+"F0.wireOp",EDGE,"E67");var subQ2=sQuery(id+"F19.wireOp",EDGE,"E133");var subQ3=sQuery(id+"F19.wireOp",EDGE,"E132");var subQ4=sQuery(id+"F19.wireOp",EDGE,"E131");var subQ5=sQuery(id+"F19.wireOp",EDGE,"E130");Q5=makeQuery(id+"F21.boolean.opBoolean","SPLIT",EDGE,{"disambiguationData":[TD([makeQuery(id+"F21.opPattern","COPY",FACE,{"derivedFrom":makeQuery(id+"F20.opExtrude","CAP_FACE",FACE,{"disambiguationData":[OSD([subQ5,subQ4,subQ3,subQ2])],"isStart":true}),"instanceName":"5"})])],"derivedFrom":makeQuery(id+"F1.opRevolve","SWEPT_EDGE",EDGE,{"disambiguationData":[OSD([subQ0,subQ1])]})});}
            var Q6;
            {var subQ0=sQuery(id+"F0.wireOp",EDGE,"E1");var subQ1=sQuery(id+"F0.wireOp",EDGE,"E67");var subQ2=sQuery(id+"F19.wireOp",EDGE,"E133");var subQ3=sQuery(id+"F19.wireOp",EDGE,"E132");var subQ4=sQuery(id+"F19.wireOp",EDGE,"E131");var subQ5=sQuery(id+"F19.wireOp",EDGE,"E130");Q6=makeQuery(id+"F21.boolean.opBoolean","SPLIT",EDGE,{"disambiguationData":[TD([makeQuery(id+"F21.opPattern","COPY",FACE,{"derivedFrom":makeQuery(id+"F20.opExtrude","CAP_FACE",FACE,{"disambiguationData":[OSD([subQ5,subQ4,subQ3,subQ2])],"isStart":true}),"instanceName":"4"})])],"derivedFrom":makeQuery(id+"F1.opRevolve","SWEPT_EDGE",EDGE,{"disambiguationData":[OSD([subQ0,subQ1])]})});}
            var Q7;
            {var subQ0=sQuery(id+"F0.wireOp",EDGE,"E1");var subQ1=sQuery(id+"F19.wireOp",EDGE,"E133");var subQ2=sQuery(id+"F19.wireOp",EDGE,"E132");var subQ3=sQuery(id+"F19.wireOp",EDGE,"E131");var subQ4=sQuery(id+"F19.wireOp",EDGE,"E130");var subQ5=sQuery(id+"F0.wireOp",EDGE,"E67");Q7=makeQuery(id+"F21.boolean.opBoolean","SPLIT",EDGE,{"disambiguationData":[TD([makeQuery(id+"F21.opPattern","COPY",FACE,{"derivedFrom":makeQuery(id+"F20.opExtrude","CAP_FACE",FACE,{"disambiguationData":[OSD([subQ4,subQ3,subQ2,subQ1])],"isStart":true}),"instanceName":"3"})])],"derivedFrom":makeQuery(id+"F1.opRevolve","SWEPT_EDGE",EDGE,{"disambiguationData":[OSD([subQ0,subQ5])]})});}
            var Q8;
            {var subQ0=sQuery(id+"F0.wireOp",EDGE,"E1");var subQ1=sQuery(id+"F19.wireOp",EDGE,"E133");var subQ2=sQuery(id+"F19.wireOp",EDGE,"E132");var subQ3=sQuery(id+"F19.wireOp",EDGE,"E131");var subQ4=sQuery(id+"F19.wireOp",EDGE,"E130");var subQ5=sQuery(id+"F0.wireOp",EDGE,"E67");Q8=makeQuery(id+"F21.boolean.opBoolean","SPLIT",EDGE,{"disambiguationData":[TD([makeQuery(id+"F21.opPattern","COPY",FACE,{"derivedFrom":makeQuery(id+"F20.opExtrude","CAP_FACE",FACE,{"disambiguationData":[OSD([subQ4,subQ3,subQ2,subQ1])],"isStart":true}),"instanceName":"2"})])],"derivedFrom":makeQuery(id+"F1.opRevolve","SWEPT_EDGE",EDGE,{"disambiguationData":[OSD([subQ0,subQ5])]})});}
            var Q9;
            {var subQ0=sQuery(id+"F0.wireOp",EDGE,"E1");var subQ1=sQuery(id+"F19.wireOp",EDGE,"E133");var subQ2=sQuery(id+"F19.wireOp",EDGE,"E132");var subQ3=sQuery(id+"F19.wireOp",EDGE,"E131");var subQ4=sQuery(id+"F19.wireOp",EDGE,"E130");var subQ5=sQuery(id+"F0.wireOp",EDGE,"E67");Q9=makeQuery(id+"F21.boolean.opBoolean","SPLIT",EDGE,{"disambiguationData":[TD([makeQuery(id+"F21.opPattern","COPY",FACE,{"derivedFrom":makeQuery(id+"F20.opExtrude","CAP_FACE",FACE,{"disambiguationData":[OSD([subQ4,subQ3,subQ2,subQ1])],"isStart":true}),"instanceName":"1"})])],"derivedFrom":makeQuery(id+"F1.opRevolve","SWEPT_EDGE",EDGE,{"disambiguationData":[OSD([subQ0,subQ5])]})});}
            var Q10;
            {var subQ0=sQuery(id+"F0.wireOp",EDGE,"E1");var subQ1=sQuery(id+"F19.wireOp",EDGE,"E133");var subQ2=sQuery(id+"F19.wireOp",EDGE,"E132");var subQ3=sQuery(id+"F19.wireOp",EDGE,"E131");var subQ4=sQuery(id+"F19.wireOp",EDGE,"E130");var subQ5=sQuery(id+"F0.wireOp",EDGE,"E67");Q10=makeQuery(id+"F21.boolean.opBoolean","SPLIT",EDGE,{"disambiguationData":[TD([makeQuery(id+"F20.opExtrude","CAP_FACE",FACE,{"disambiguationData":[OSD([subQ4,subQ3,subQ2,subQ1])],"isStart":true})])],"derivedFrom":makeQuery(id+"F1.opRevolve","SWEPT_EDGE",EDGE,{"disambiguationData":[OSD([subQ0,subQ5])]})});}
            var Q11;
            {var subQ0=sQuery(id+"F0.wireOp",EDGE,"E1");var subQ1=sQuery(id+"F19.wireOp",EDGE,"E133");var subQ2=sQuery(id+"F19.wireOp",EDGE,"E132");var subQ3=sQuery(id+"F19.wireOp",EDGE,"E131");var subQ4=sQuery(id+"F19.wireOp",EDGE,"E130");var subQ5=sQuery(id+"F0.wireOp",EDGE,"E67");Q11=makeQuery(id+"F21.boolean.opBoolean","SPLIT",EDGE,{"disambiguationData":[TD([makeQuery(id+"F20.opExtrude","CAP_FACE",FACE,{"disambiguationData":[OSD([subQ4,subQ3,subQ2,subQ1])],"isStart":false})])],"derivedFrom":makeQuery(id+"F1.opRevolve","SWEPT_EDGE",EDGE,{"disambiguationData":[OSD([subQ0,subQ5])]})});}
            fillet(context, id + "F40", {"entities" : qUnion([Q0, Q1, Q2, Q3, Q4, Q5, Q6, Q7, Q8, Q9, Q10, Q11]), "radius" : 1.27 * mm, "tangentPropagation" : true, "allowEdgeOverflow" : false});
        }
        {
            var Q0;
            Q0=qCreatedBy(makeId("Top.planeOp"),FACE);
            var sketch = newSketch(context, id + "F41", { "sketchPlane" : qUnion([Q0])});
            skLineSegment(sketch, "E207.bottom", {"start": v(-6.35, 186.06) * mm, "end": v(6.35, 186.06) * mm});
            skLineSegment(sketch, "E207.top", {"start": v(-6.35, 154.69) * mm, "end": v(6.35, 154.69) * mm});
            skLineSegment(sketch, "E207.left", {"start": v(-6.35, 186.06) * mm, "end": v(-6.35, 154.69) * mm});
            skLineSegment(sketch, "E207.right", {"start": v(6.35, 186.06) * mm, "end": v(6.35, 154.69) * mm});
            skSolve(sketch);
        }
        {
            var Q0;
            Q0 = qSketchRegion(id + "F41", true);
            extrude(context, id + "F42", {"entities" : qUnion([Q0]), "operationType" : NewBodyOperationType.ADD, "depth" : 27.94 * mm});
        }
        {
            var Q0;
            Q0=makeQuery(id+"F42.opExtrude","CAP_FACE",FACE,{"disambiguationData":[OSD([sQuery(id+"F41.wireOp",EDGE,"E207.bottom"),sQuery(id+"F41.wireOp",EDGE,"E207.top"),sQuery(id+"F41.wireOp",EDGE,"E207.left"),sQuery(id+"F41.wireOp",EDGE,"E207.right")])],"isStart":false});
            var sketch = newSketch(context, id + "F43", { "sketchPlane" : qUnion([Q0])});
            skLineSegment(sketch, "E208.bottom", {"start": v(-5.08, 184.78) * mm, "end": v(5.08, 184.78) * mm});
            skLineSegment(sketch, "E208.top", {"start": v(-5.08, 155.96) * mm, "end": v(5.08, 155.96) * mm});
            skLineSegment(sketch, "E208.left", {"start": v(-5.08, 184.78) * mm, "end": v(-5.08, 155.96) * mm});
            skLineSegment(sketch, "E208.right", {"start": v(5.08, 184.78) * mm, "end": v(5.08, 155.96) * mm});
            skLineSegment(sketch, "E209.bottom", {"start": v(-4.45, 184.15) * mm, "end": v(4.44, 184.15) * mm});
            skLineSegment(sketch, "E209.top", {"start": v(-4.45, 156.6) * mm, "end": v(4.44, 156.6) * mm});
            skLineSegment(sketch, "E209.left", {"start": v(-4.45, 184.15) * mm, "end": v(-4.45, 156.6) * mm});
            skLineSegment(sketch, "E209.right", {"start": v(4.44, 184.15) * mm, "end": v(4.44, 156.6) * mm});
            skSolve(sketch);
        }
        {
            var Q0;
            Q0 = qSketchRegion(id + "F43", true);
            extrude(context, id + "F44", {"entities" : qUnion([Q0]), "operationType" : NewBodyOperationType.REMOVE, "oppositeDirection" : true, "depth" : 2.54 * mm});
        }
        {
            var Q0;
            Q0=makeQuery(id+"F44.boolean.opBoolean","SPLIT",FACE,{"disambiguationData":[TD([makeQuery(id+"F44.opExtrude","SWEPT_FACE",FACE,{"disambiguationData":[OSD([sQuery(id+"F43.wireOp",EDGE,"E209.bottom")])]})])],"derivedFrom":makeQuery(id+"F42.opExtrude","CAP_FACE",FACE,{"disambiguationData":[OSD([sQuery(id+"F41.wireOp",EDGE,"E207.bottom"),sQuery(id+"F41.wireOp",EDGE,"E207.top"),sQuery(id+"F41.wireOp",EDGE,"E207.left"),sQuery(id+"F41.wireOp",EDGE,"E207.right")])],"isStart":false})});
            var sketch = newSketch(context, id + "F45", { "sketchPlane" : qUnion([Q0])});
            skLineSegment(sketch, "E210", {"start": v(0, 184.15) * mm, "end": v(0, 156.6) * mm, "construction": true});
            skLineSegment(sketch, "E211", {"start": v(-4.45, 179.7) * mm, "end": v(4.44, 179.7) * mm, "construction": true});
            skLineSegment(sketch, "E212", {"start": v(-4.45, 161.04) * mm, "end": v(4.44, 161.04) * mm, "construction": true});
            skLineSegment(sketch, "E213.rect.bottom", {"start": v(1.61, 179.45) * mm, "end": v(-1.61, 179.45) * mm});
            skLineSegment(sketch, "E213.rect.top", {"start": v(1.61, 179.7) * mm, "end": v(-1.61, 179.7) * mm});
            skPoint(sketch, "E213.rect.middle", {"position": v(0, 179.58) * mm});
            skLineSegment(sketch, "E214.1.0.0", {"start": v(1.9, 178.82) * mm, "end": v(-1.9, 178.82) * mm});
            skLineSegment(sketch, "E214.1.0.1", {"start": v(-1.9, 178.82) * mm, "end": v(-1.9, 179.07) * mm});
            skLineSegment(sketch, "E214.1.0.2", {"start": v(1.9, 178.82) * mm, "end": v(1.9, 179.07) * mm});
            skLineSegment(sketch, "E214.1.0.3", {"start": v(1.9, 179.07) * mm, "end": v(-1.9, 179.07) * mm});
            skLineSegment(sketch, "E214.2.0.0", {"start": v(1.9, 178.18) * mm, "end": v(-1.9, 178.18) * mm});
            skLineSegment(sketch, "E214.2.0.1", {"start": v(-1.9, 178.18) * mm, "end": v(-1.9, 178.44) * mm});
            skLineSegment(sketch, "E214.2.0.2", {"start": v(1.9, 178.18) * mm, "end": v(1.9, 178.44) * mm});
            skLineSegment(sketch, "E214.2.0.3", {"start": v(1.9, 178.44) * mm, "end": v(-1.9, 178.44) * mm});
            skLineSegment(sketch, "E214.3.0.0", {"start": v(1.9, 177.55) * mm, "end": v(-1.9, 177.55) * mm});
            skLineSegment(sketch, "E214.3.0.1", {"start": v(-1.9, 177.55) * mm, "end": v(-1.9, 177.8) * mm});
            skLineSegment(sketch, "E214.3.0.2", {"start": v(1.9, 177.55) * mm, "end": v(1.9, 177.8) * mm});
            skLineSegment(sketch, "E214.3.0.3", {"start": v(1.9, 177.8) * mm, "end": v(-1.9, 177.8) * mm});
            skLineSegment(sketch, "E214.4.0.0", {"start": v(1.9, 176.91) * mm, "end": v(-1.9, 176.91) * mm});
            skLineSegment(sketch, "E214.4.0.1", {"start": v(-1.9, 176.91) * mm, "end": v(-1.9, 177.17) * mm});
            skLineSegment(sketch, "E214.4.0.2", {"start": v(1.9, 176.91) * mm, "end": v(1.9, 177.17) * mm});
            skLineSegment(sketch, "E214.4.0.3", {"start": v(1.9, 177.17) * mm, "end": v(-1.9, 177.17) * mm});
            skLineSegment(sketch, "E214.5.0.0", {"start": v(1.9, 176.28) * mm, "end": v(-1.9, 176.28) * mm});
            skLineSegment(sketch, "E214.5.0.1", {"start": v(-1.9, 176.28) * mm, "end": v(-1.9, 176.53) * mm});
            skLineSegment(sketch, "E214.5.0.2", {"start": v(1.9, 176.28) * mm, "end": v(1.9, 176.53) * mm});
            skLineSegment(sketch, "E214.5.0.3", {"start": v(1.9, 176.53) * mm, "end": v(-1.9, 176.53) * mm});
            skLineSegment(sketch, "E214.6.0.0", {"start": v(1.9, 175.64) * mm, "end": v(-1.9, 175.64) * mm});
            skLineSegment(sketch, "E214.6.0.1", {"start": v(-1.9, 175.64) * mm, "end": v(-1.9, 175.9) * mm});
            skLineSegment(sketch, "E214.6.0.2", {"start": v(1.9, 175.64) * mm, "end": v(1.9, 175.9) * mm});
            skLineSegment(sketch, "E214.6.0.3", {"start": v(1.9, 175.9) * mm, "end": v(-1.9, 175.9) * mm});
            skLineSegment(sketch, "E214.7.0.0", {"start": v(1.9, 175) * mm, "end": v(-1.9, 175) * mm});
            skLineSegment(sketch, "E214.7.0.1", {"start": v(-1.9, 175) * mm, "end": v(-1.9, 175.26) * mm});
            skLineSegment(sketch, "E214.7.0.2", {"start": v(1.9, 175) * mm, "end": v(1.9, 175.26) * mm});
            skLineSegment(sketch, "E214.7.0.3", {"start": v(1.9, 175.26) * mm, "end": v(-1.9, 175.26) * mm});
            skLineSegment(sketch, "E214.8.0.0", {"start": v(1.9, 174.37) * mm, "end": v(-1.91, 174.37) * mm});
            skLineSegment(sketch, "E214.8.0.1", {"start": v(-1.91, 174.37) * mm, "end": v(-1.91, 174.63) * mm});
            skLineSegment(sketch, "E214.8.0.2", {"start": v(1.9, 174.37) * mm, "end": v(1.9, 174.63) * mm});
            skLineSegment(sketch, "E214.8.0.3", {"start": v(1.9, 174.63) * mm, "end": v(-1.91, 174.63) * mm});
            skLineSegment(sketch, "E214.9.0.0", {"start": v(1.9, 173.74) * mm, "end": v(-1.91, 173.74) * mm});
            skLineSegment(sketch, "E214.9.0.1", {"start": v(-1.91, 173.74) * mm, "end": v(-1.91, 174) * mm});
            skLineSegment(sketch, "E214.9.0.2", {"start": v(1.9, 173.74) * mm, "end": v(1.9, 174) * mm});
            skLineSegment(sketch, "E214.9.0.3", {"start": v(1.9, 174) * mm, "end": v(-1.91, 174) * mm});
            skLineSegment(sketch, "E214.10.0.0", {"start": v(1.9, 173.1) * mm, "end": v(-1.91, 173.1) * mm});
            skLineSegment(sketch, "E214.10.0.1", {"start": v(-1.91, 173.1) * mm, "end": v(-1.91, 173.36) * mm});
            skLineSegment(sketch, "E214.10.0.2", {"start": v(1.9, 173.1) * mm, "end": v(1.9, 173.36) * mm});
            skLineSegment(sketch, "E214.10.0.3", {"start": v(1.9, 173.36) * mm, "end": v(-1.91, 173.36) * mm});
            skLineSegment(sketch, "E214.11.0.0", {"start": v(1.9, 172.47) * mm, "end": v(-1.91, 172.47) * mm});
            skLineSegment(sketch, "E214.11.0.1", {"start": v(-1.91, 172.47) * mm, "end": v(-1.91, 172.72) * mm});
            skLineSegment(sketch, "E214.11.0.2", {"start": v(1.9, 172.47) * mm, "end": v(1.9, 172.72) * mm});
            skLineSegment(sketch, "E214.11.0.3", {"start": v(1.9, 172.72) * mm, "end": v(-1.91, 172.72) * mm});
            skLineSegment(sketch, "E214.12.0.0", {"start": v(1.9, 171.83) * mm, "end": v(-1.91, 171.83) * mm});
            skLineSegment(sketch, "E214.12.0.1", {"start": v(-1.91, 171.83) * mm, "end": v(-1.91, 172.09) * mm});
            skLineSegment(sketch, "E214.12.0.2", {"start": v(1.9, 171.83) * mm, "end": v(1.9, 172.09) * mm});
            skLineSegment(sketch, "E214.12.0.3", {"start": v(1.9, 172.09) * mm, "end": v(-1.91, 172.09) * mm});
            skLineSegment(sketch, "E214.13.0.0", {"start": v(1.9, 171.2) * mm, "end": v(-1.91, 171.2) * mm});
            skLineSegment(sketch, "E214.13.0.1", {"start": v(-1.91, 171.2) * mm, "end": v(-1.91, 171.45) * mm});
            skLineSegment(sketch, "E214.13.0.2", {"start": v(1.9, 171.2) * mm, "end": v(1.9, 171.45) * mm});
            skLineSegment(sketch, "E214.13.0.3", {"start": v(1.9, 171.45) * mm, "end": v(-1.91, 171.45) * mm});
            skLineSegment(sketch, "E214.14.0.0", {"start": v(1.9, 170.56) * mm, "end": v(-1.91, 170.56) * mm});
            skLineSegment(sketch, "E214.14.0.1", {"start": v(-1.91, 170.56) * mm, "end": v(-1.91, 170.82) * mm});
            skLineSegment(sketch, "E214.14.0.2", {"start": v(1.9, 170.56) * mm, "end": v(1.9, 170.82) * mm});
            skLineSegment(sketch, "E214.14.0.3", {"start": v(1.9, 170.82) * mm, "end": v(-1.91, 170.82) * mm});
            skLineSegment(sketch, "E214.15.0.0", {"start": v(1.9, 169.93) * mm, "end": v(-1.91, 169.93) * mm});
            skLineSegment(sketch, "E214.15.0.1", {"start": v(-1.91, 169.93) * mm, "end": v(-1.91, 170.18) * mm});
            skLineSegment(sketch, "E214.15.0.2", {"start": v(1.9, 169.93) * mm, "end": v(1.9, 170.18) * mm});
            skLineSegment(sketch, "E214.15.0.3", {"start": v(1.9, 170.18) * mm, "end": v(-1.91, 170.18) * mm});
            skLineSegment(sketch, "E214.16.0.0", {"start": v(1.9, 169.3) * mm, "end": v(-1.92, 169.3) * mm});
            skLineSegment(sketch, "E214.16.0.1", {"start": v(-1.92, 169.3) * mm, "end": v(-1.92, 169.55) * mm});
            skLineSegment(sketch, "E214.16.0.2", {"start": v(1.9, 169.3) * mm, "end": v(1.9, 169.55) * mm});
            skLineSegment(sketch, "E214.16.0.3", {"start": v(1.9, 169.55) * mm, "end": v(-1.92, 169.55) * mm});
            skLineSegment(sketch, "E214.17.0.0", {"start": v(1.9, 168.66) * mm, "end": v(-1.92, 168.66) * mm});
            skLineSegment(sketch, "E214.17.0.1", {"start": v(-1.92, 168.66) * mm, "end": v(-1.92, 168.91) * mm});
            skLineSegment(sketch, "E214.17.0.2", {"start": v(1.9, 168.66) * mm, "end": v(1.9, 168.91) * mm});
            skLineSegment(sketch, "E214.17.0.3", {"start": v(1.9, 168.91) * mm, "end": v(-1.92, 168.91) * mm});
            skLineSegment(sketch, "E214.18.0.0", {"start": v(1.9, 168.02) * mm, "end": v(-1.92, 168.02) * mm});
            skLineSegment(sketch, "E214.18.0.1", {"start": v(-1.92, 168.02) * mm, "end": v(-1.92, 168.28) * mm});
            skLineSegment(sketch, "E214.18.0.2", {"start": v(1.9, 168.02) * mm, "end": v(1.9, 168.28) * mm});
            skLineSegment(sketch, "E214.18.0.3", {"start": v(1.9, 168.28) * mm, "end": v(-1.92, 168.28) * mm});
            skLineSegment(sketch, "E214.19.0.0", {"start": v(1.9, 167.39) * mm, "end": v(-1.92, 167.39) * mm});
            skLineSegment(sketch, "E214.19.0.1", {"start": v(-1.92, 167.39) * mm, "end": v(-1.92, 167.64) * mm});
            skLineSegment(sketch, "E214.19.0.2", {"start": v(1.9, 167.39) * mm, "end": v(1.9, 167.64) * mm});
            skLineSegment(sketch, "E214.19.0.3", {"start": v(1.9, 167.64) * mm, "end": v(-1.92, 167.64) * mm});
            skLineSegment(sketch, "E214.20.0.0", {"start": v(1.9, 166.75) * mm, "end": v(-1.92, 166.75) * mm});
            skLineSegment(sketch, "E214.20.0.1", {"start": v(-1.92, 166.75) * mm, "end": v(-1.92, 167) * mm});
            skLineSegment(sketch, "E214.20.0.2", {"start": v(1.9, 166.75) * mm, "end": v(1.9, 167) * mm});
            skLineSegment(sketch, "E214.20.0.3", {"start": v(1.9, 167) * mm, "end": v(-1.92, 167) * mm});
            skLineSegment(sketch, "E214.21.0.0", {"start": v(1.9, 166.12) * mm, "end": v(-1.92, 166.12) * mm});
            skLineSegment(sketch, "E214.21.0.1", {"start": v(-1.92, 166.12) * mm, "end": v(-1.92, 166.37) * mm});
            skLineSegment(sketch, "E214.21.0.2", {"start": v(1.9, 166.12) * mm, "end": v(1.9, 166.37) * mm});
            skLineSegment(sketch, "E214.21.0.3", {"start": v(1.9, 166.37) * mm, "end": v(-1.92, 166.37) * mm});
            skLineSegment(sketch, "E214.22.0.0", {"start": v(1.9, 165.48) * mm, "end": v(-1.92, 165.48) * mm});
            skLineSegment(sketch, "E214.22.0.1", {"start": v(-1.92, 165.48) * mm, "end": v(-1.92, 165.74) * mm});
            skLineSegment(sketch, "E214.22.0.2", {"start": v(1.9, 165.48) * mm, "end": v(1.9, 165.74) * mm});
            skLineSegment(sketch, "E214.22.0.3", {"start": v(1.9, 165.74) * mm, "end": v(-1.92, 165.74) * mm});
            skLineSegment(sketch, "E214.23.0.0", {"start": v(1.89, 164.85) * mm, "end": v(-1.92, 164.85) * mm});
            skLineSegment(sketch, "E214.23.0.1", {"start": v(-1.92, 164.85) * mm, "end": v(-1.92, 165.1) * mm});
            skLineSegment(sketch, "E214.23.0.2", {"start": v(1.89, 164.85) * mm, "end": v(1.89, 165.1) * mm});
            skLineSegment(sketch, "E214.23.0.3", {"start": v(1.89, 165.1) * mm, "end": v(-1.92, 165.1) * mm});
            skLineSegment(sketch, "E214.24.0.0", {"start": v(1.89, 164.21) * mm, "end": v(-1.92, 164.21) * mm});
            skLineSegment(sketch, "E214.24.0.1", {"start": v(-1.92, 164.21) * mm, "end": v(-1.92, 164.47) * mm});
            skLineSegment(sketch, "E214.24.0.2", {"start": v(1.89, 164.21) * mm, "end": v(1.89, 164.47) * mm});
            skLineSegment(sketch, "E214.24.0.3", {"start": v(1.89, 164.47) * mm, "end": v(-1.92, 164.47) * mm});
            skLineSegment(sketch, "E214.25.0.0", {"start": v(1.89, 163.58) * mm, "end": v(-1.92, 163.58) * mm});
            skLineSegment(sketch, "E214.25.0.1", {"start": v(-1.92, 163.58) * mm, "end": v(-1.92, 163.83) * mm});
            skLineSegment(sketch, "E214.25.0.2", {"start": v(1.89, 163.58) * mm, "end": v(1.89, 163.83) * mm});
            skLineSegment(sketch, "E214.25.0.3", {"start": v(1.89, 163.83) * mm, "end": v(-1.92, 163.83) * mm});
            skLineSegment(sketch, "E214.26.0.0", {"start": v(1.89, 162.94) * mm, "end": v(-1.92, 162.94) * mm});
            skLineSegment(sketch, "E214.26.0.1", {"start": v(-1.92, 162.94) * mm, "end": v(-1.92, 163.2) * mm});
            skLineSegment(sketch, "E214.26.0.2", {"start": v(1.89, 162.94) * mm, "end": v(1.89, 163.2) * mm});
            skLineSegment(sketch, "E214.26.0.3", {"start": v(1.89, 163.2) * mm, "end": v(-1.92, 163.2) * mm});
            skLineSegment(sketch, "E214.27.0.0", {"start": v(1.89, 162.3) * mm, "end": v(-1.92, 162.3) * mm});
            skLineSegment(sketch, "E214.27.0.1", {"start": v(-1.92, 162.3) * mm, "end": v(-1.92, 162.56) * mm});
            skLineSegment(sketch, "E214.27.0.2", {"start": v(1.89, 162.3) * mm, "end": v(1.89, 162.56) * mm});
            skLineSegment(sketch, "E214.27.0.3", {"start": v(1.89, 162.56) * mm, "end": v(-1.92, 162.56) * mm});
            skLineSegment(sketch, "E214.28.0.0", {"start": v(1.89, 161.67) * mm, "end": v(-1.92, 161.67) * mm});
            skLineSegment(sketch, "E214.28.0.1", {"start": v(-1.92, 161.67) * mm, "end": v(-1.92, 161.93) * mm});
            skLineSegment(sketch, "E214.28.0.2", {"start": v(1.89, 161.67) * mm, "end": v(1.89, 161.93) * mm});
            skLineSegment(sketch, "E214.28.0.3", {"start": v(1.89, 161.93) * mm, "end": v(-1.92, 161.93) * mm});
            skLineSegment(sketch, "E214.29.0.0", {"start": v(1.6, 161.04) * mm, "end": v(-1.63, 161.04) * mm});
            skLineSegment(sketch, "E214.29.0.3", {"start": v(1.6, 161.3) * mm, "end": v(-1.63, 161.3) * mm});
            skLineSegment(sketch, "E214.direction1", {"start": v(-1.9, 179.45) * mm, "end": v(-1.9, 178.82) * mm, "construction": true});
            skArc(sketch, "E215", {"start": v(-1.61, 179.7) * mm, "mid": v(-2.22, 179.58) * mm, "end": v(-1.61, 179.45) * mm});
            skArc(sketch, "E216", {"start": v(1.61, 179.45) * mm, "mid": v(2.22, 179.58) * mm, "end": v(1.61, 179.7) * mm});
            skArc(sketch, "E217", {"start": v(-1.63, 161.3) * mm, "mid": v(-2.24, 161.16) * mm, "end": v(-1.63, 161.04) * mm});
            skArc(sketch, "E218", {"start": v(1.6, 161.04) * mm, "mid": v(2.2, 161.16) * mm, "end": v(1.6, 161.3) * mm});
            skPoint(sketch, "E213.rect.right.end.orphan", {"position": v(-1.9, 179.7) * mm});
            skPoint(sketch, "E219.orphan", {"position": v(1.9, 179.7) * mm});
            skPoint(sketch, "E213.rect.left.start.orphan", {"position": v(1.9, 179.45) * mm});
            skPoint(sketch, "E220.orphan", {"position": v(-1.92, 161.04) * mm});
            skPoint(sketch, "E214.29.0.1.end.orphan", {"position": v(-1.92, 161.3) * mm});
            skPoint(sketch, "E221.orphan", {"position": v(1.89, 161.3) * mm});
            skPoint(sketch, "E214.29.0.2.start.orphan", {"position": v(1.89, 161.04) * mm});
            skLineSegment(sketch, "E222.rect.bottom", {"start": v(3.5, 180.6) * mm, "end": v(-3.5, 180.6) * mm});
            skLineSegment(sketch, "E222.rect.top", {"start": v(3.5, 183.26) * mm, "end": v(-3.5, 183.26) * mm});
            skLineSegment(sketch, "E222.rect.left", {"start": v(3.5, 180.6) * mm, "end": v(3.5, 183.26) * mm});
            skLineSegment(sketch, "E222.rect.right", {"start": v(-3.5, 180.6) * mm, "end": v(-3.5, 183.26) * mm});
            skPoint(sketch, "E222.rect.middle", {"position": v(0, 181.93) * mm});
            skLineSegment(sketch, "E223.rect.bottom", {"start": v(3.24, 180.85) * mm, "end": v(-3.24, 180.85) * mm});
            skLineSegment(sketch, "E223.rect.top", {"start": v(3.24, 183) * mm, "end": v(-3.24, 183) * mm});
            skLineSegment(sketch, "E223.rect.left", {"start": v(3.24, 180.85) * mm, "end": v(3.24, 183) * mm});
            skLineSegment(sketch, "E223.rect.right", {"start": v(-3.24, 180.85) * mm, "end": v(-3.24, 183) * mm});
            skLineSegment(sketch, "E224.rect.bottom", {"start": v(3.5, 157.48) * mm, "end": v(-3.5, 157.48) * mm});
            skLineSegment(sketch, "E224.rect.top", {"start": v(3.5, 160.15) * mm, "end": v(-3.5, 160.15) * mm});
            skLineSegment(sketch, "E224.rect.left", {"start": v(3.5, 157.48) * mm, "end": v(3.5, 160.15) * mm});
            skLineSegment(sketch, "E224.rect.right", {"start": v(-3.5, 157.48) * mm, "end": v(-3.5, 160.15) * mm});
            skPoint(sketch, "E224.rect.middle", {"position": v(0, 158.81) * mm});
            skLineSegment(sketch, "E225.rect.bottom", {"start": v(3.24, 157.73) * mm, "end": v(-3.24, 157.73) * mm});
            skLineSegment(sketch, "E225.rect.top", {"start": v(3.24, 159.9) * mm, "end": v(-3.24, 159.9) * mm});
            skLineSegment(sketch, "E225.rect.left", {"start": v(3.24, 157.73) * mm, "end": v(3.24, 159.9) * mm});
            skLineSegment(sketch, "E225.rect.right", {"start": v(-3.24, 157.73) * mm, "end": v(-3.24, 159.9) * mm});
            skSolve(sketch);
        }
        {
            var Q0;
            Q0 = qSketchRegion(id + "F45", true);
            extrude(context, id + "F46", {"entities" : qUnion([Q0]), "operationType" : NewBodyOperationType.REMOVE, "oppositeDirection" : true, "depth" : 1.27 * mm});
        }
        {
            var Q0;
            Q0=makeQuery(id+"F42.opExtrude","CAP_EDGE",EDGE,{"disambiguationData":[OSD([sQuery(id+"F41.wireOp",EDGE,"E207.left")])],"isStart":false});
            var Q1;
            Q1=makeQuery(id+"F42.opExtrude","CAP_EDGE",EDGE,{"disambiguationData":[OSD([sQuery(id+"F41.wireOp",EDGE,"E207.top")])],"isStart":false});
            var Q2;
            Q2=makeQuery(id+"F42.opExtrude","CAP_EDGE",EDGE,{"disambiguationData":[OSD([sQuery(id+"F41.wireOp",EDGE,"E207.right")])],"isStart":false});
            var Q3;
            Q3=makeQuery(id+"F42.opExtrude","CAP_EDGE",EDGE,{"disambiguationData":[OSD([sQuery(id+"F41.wireOp",EDGE,"E207.bottom")])],"isStart":false});
            chamfer(context, id + "F47", {"entities" : qUnion([Q0, Q1, Q2, Q3]), "width" : 0.64 * mm, "tangentPropagation" : true});
        }
    });
